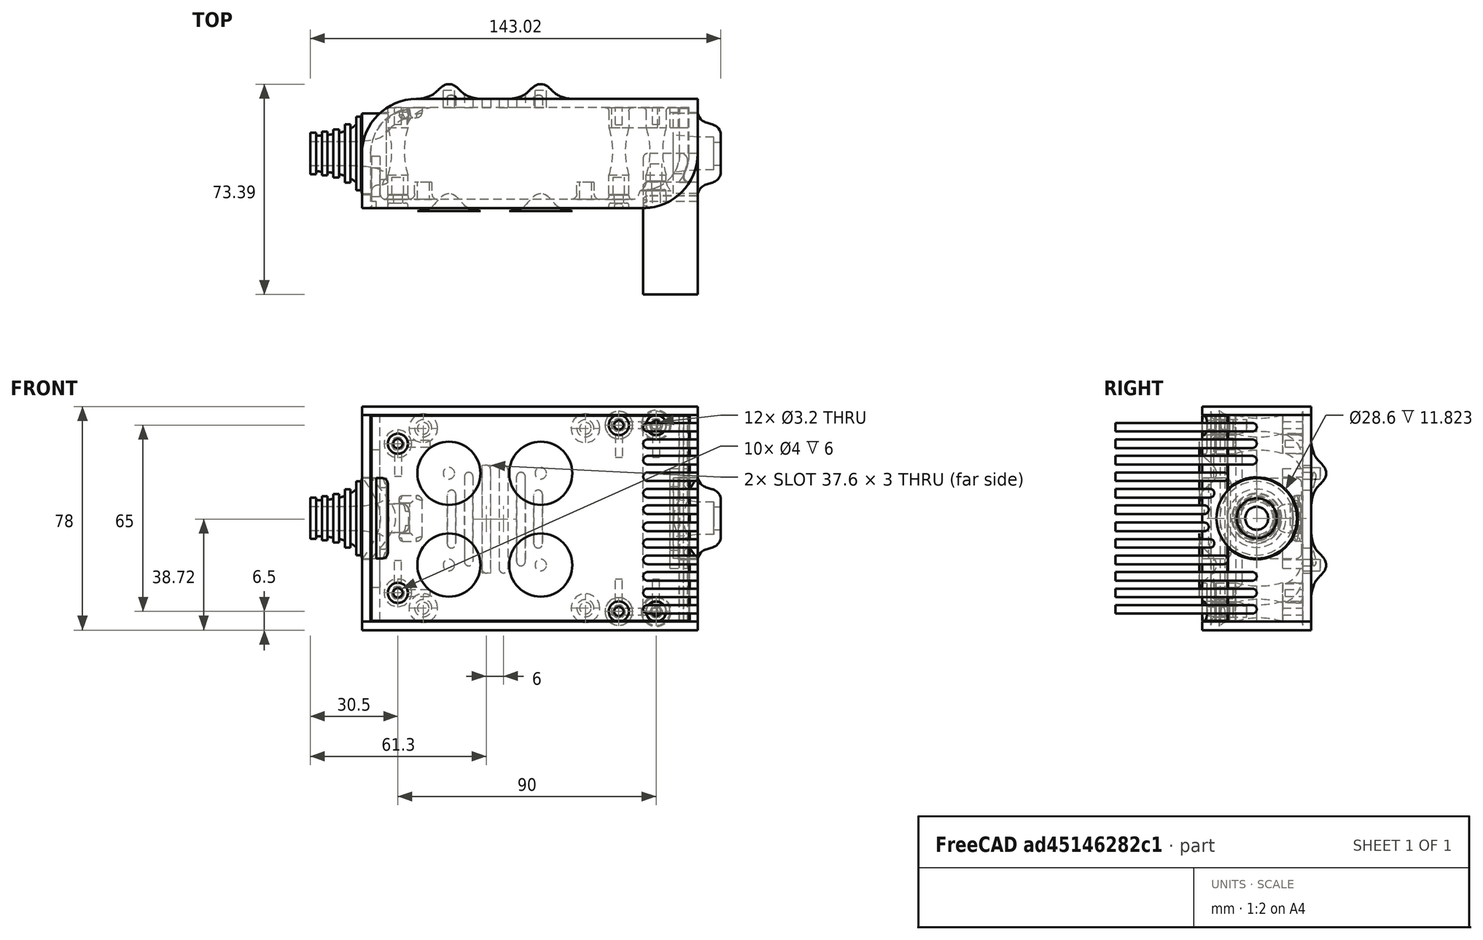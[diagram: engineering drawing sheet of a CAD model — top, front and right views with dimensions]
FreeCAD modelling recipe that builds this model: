
FCSTD DOCUMENT  (FreeCAD 0.19R0.19.2)
Label: enclosure_116
License: All rights reserved
LicenseURL: http://en.wikipedia.org/wiki/All_rights_reserved
objects: Part::Feature×72, Part::Revolution×72, Part::MultiFuse×53, Sketcher::SketchObject×31, Part::Fillet×23, Part::Cylinder×22, Part::Extrusion×20, Part::Cut×20, Part::Box×12, App::MeasureDistance×4
note: 325 computed .brp shape members not serialized (recipe doc carries the construction recipe); baked Part::Feature solids carry a one-line shape summary decoded from their .brp

FEATURE [Sketcher::SketchObject] Sketch  label="topSketch"
  FullyConstrained = true
  sketch-geometry (13):
    g0: LineSegment StartX=117 StartY=19 StartZ=0 EndX=117 EndY=38 EndZ=0
    g1: ArcOfCircle CenterX=98 CenterY=19 CenterZ=0 NormalX=0 NormalY=0 NormalZ=1 AngleXU=0 Radius=19 StartAngle=5.7297 EndAngle=6.28319
    g2: LineSegment StartX=0 StartY=3 StartZ=0 EndX=0 EndY=19 EndZ=0
    g3: LineSegment StartX=19 StartY=38 StartZ=0 EndX=117 EndY=38 EndZ=0
    g4: ArcOfCircle CenterX=19 CenterY=19 CenterZ=0 NormalX=0 NormalY=0 NormalZ=1 AngleXU=0 Radius=19 StartAngle=1.5708 EndAngle=3.14159
    g5: ArcOfCircle CenterX=19 CenterY=19 CenterZ=0 NormalX=0 NormalY=0 NormalZ=1 AngleXU=0 Radius=16 StartAngle=1.5708 EndAngle=3.14159
    g6: ArcOfCircle CenterX=98 CenterY=19 CenterZ=0 NormalX=0 NormalY=0 NormalZ=1 AngleXU=0 Radius=16 StartAngle=5.60905 EndAngle=6.28319
    g7: LineSegment StartX=114 StartY=19 StartZ=0 EndX=114 EndY=35 EndZ=0
    g8: LineSegment StartX=110.5 StartY=9.01251 StartZ=0 EndX=114.163 EndY=9.01251 EndZ=0
    g9: LineSegment StartX=114 StartY=35 StartZ=0 EndX=19 EndY=35 EndZ=0
    g10: LineSegment StartX=0 StartY=3 StartZ=0 EndX=0 EndY=0 EndZ=0
    g11: LineSegment StartX=3 StartY=0 StartZ=0 EndX=0 EndY=0 EndZ=0
    g12: LineSegment StartX=3 StartY=19 StartZ=0 EndX=3 EndY=0 EndZ=0
  constraints (33):
    c: Vertical(g0)
    c: Distance(g0) = 19
    c: Block(g0)
    c: Coincident(g1,g0)
    c: Block(g1)
    c: Vertical(g2)
    c: Block(g2)
    c: Coincident(g3,g0)
    c: Horizontal(g3)
    c: Distance(g3) = 98
    c: Coincident(g4,g3)
    c: Coincident(g4,g2)
    c: Block(g4)
    c: Coincident(g5,g4)
    c: Coincident(g6,g1)
    c: Block(g6)
    c: Block(g5)
    c: Coincident(g7,g6)
    c: Vertical(g7)
    c: Coincident(g8,g6)
    c: Coincident(g8,g1)
    c: Coincident(g9,g7)
    c: Coincident(g9,g5)
    c: Horizontal(g9)
    c: Tangent(g9,g5)
    c: Coincident(g10,g2)
    c: Distance(g10) = 3
    c: Vertical(g10)
    c: Coincident(g11,g10)
    c: Horizontal(g11)
    c: Coincident(g12,g5)
    c: Coincident(g12,g11)
    c: Vertical(g12)
FEATURE [Sketcher::SketchObject] Sketch001  label="bottomSketch"
  FullyConstrained = true
  sketch-geometry (32):
    g0: LineSegment StartX=3.3 StartY=-6.03275e-07 StartZ=0 EndX=98 EndY=-6.03275e-07 EndZ=0
    g1: ArcOfCircle CenterX=98 CenterY=19 CenterZ=0 NormalX=0 NormalY=0 NormalZ=1 AngleXU=0 Radius=19 StartAngle=4.71239 EndAngle=5.71103
    g2: LineSegment StartX=6.3 StartY=8 StartZ=0 EndX=3.3 EndY=8 EndZ=0
    g3: LineSegment StartX=3.3 StartY=8 StartZ=0 EndX=3.3 EndY=-6.03275e-07 EndZ=0
    g4: ArcOfCircle CenterX=8.3 CenterY=5 CenterZ=0 NormalX=0 NormalY=0 NormalZ=1 AngleXU=0 Radius=2 StartAngle=3.14159 EndAngle=4.71239
    g5: LineSegment StartX=6.3 StartY=8 StartZ=0 EndX=6.3 EndY=5 EndZ=0
    g6: ArcOfCircle CenterX=98 CenterY=19 CenterZ=0 NormalX=0 NormalY=0 NormalZ=1 AngleXU=0 Radius=12.7 StartAngle=4.71239 EndAngle=6.28319
    g7: LineSegment StartX=94.7 StartY=3 StartZ=0 EndX=8.3 EndY=3 EndZ=0
    g8-g12: Circle x5 (B-spline internal-alignment scaffolding for g13; pole/knot coordinates omitted)
    g13: BSplineCurve PolesCount=5 KnotsCount=3 Degree=3 IsPeriodic=0
    g14: GeomPoint X=98 Y=6.3 Z=0
    g15: GeomPoint X=96.3938 Y=4.71946 Z=0
    g16: GeomPoint X=94.7 Y=3 Z=0
    g17-g23: Circle x7 (B-spline internal-alignment scaffolding for g24; pole/knot coordinates omitted)
    g24: BSplineCurve PolesCount=7 KnotsCount=5 Degree=3 IsPeriodic=0
    g25-g29: GeomPoint x5 (B-spline internal-alignment scaffolding for g24; pole/knot coordinates omitted)
    g30: ArcOfCircle CenterX=98 CenterY=19 CenterZ=0 NormalX=0 NormalY=0 NormalZ=1 AngleXU=0 Radius=15.7 StartAngle=5.81226 EndAngle=6.28319
    g31: LineSegment StartX=110.7 StartY=19 StartZ=0 EndX=113.7 EndY=19 EndZ=0
  constraints (41):
    c: Horizontal(g0)
    c: Coincident(g1,g0)
    c: Block(g1)
    c: Horizontal(g2)
    c: Distance(g2) = 3
    c: Coincident(g3,g2)
    c: Vertical(g3)
    c: Coincident(g3,g0)
    c: Block(g4)
    c: Block(g2)
    c: Coincident(g5,g2)
    c: Coincident(g5,g4)
    c: Vertical(g5)
    c: Coincident(g6,g1)
    c: Block(g6)
    c: Coincident(g7,g4)
    c: Horizontal(g7)
    c: Block(g0)
    c: Block(g7)
    c: Block(g3)
    c: Coincident(g13,g6)
    c: Weight(g8) = 1
    c: Equal(g8, g9-g12) x4
    c: Coincident(g13,g7)
    c: InternalAlignment(g8-g12 -> g13) x5
    c: InternalAlignment(g14,g13)
    c: InternalAlignment(g15,g13)
    c: InternalAlignment(g16,g13)
    c: Block(g13)
    c: Weight(g17) = 1
    c: Equal(g17, g18-g23) x6
    c: Coincident(g24,g1)
    c: InternalAlignment(g17-g23 -> g24) x7
    c: InternalAlignment(g25-g29 -> g24) x5
    c: Block(g24)
    c: Coincident(g30,g24)
    c: Coincident(g31,g6)
    c: Coincident(g31,g30)
    c: Horizontal(g31)
    c: Block(g31)
    c: Block(g30)
FEATURE [Part::Extrusion] Extrude  label="top"
  Base = -> Sketch
  Dir = (0,0,1)
  DirMode = 2
  FaceMakerClass = Part::FaceMakerBullseye
  LengthFwd = 72
  LengthRev = 0
  Solid = true
  Symmetric = false
FEATURE [Part::Extrusion] Extrude001  label="bottom"
  Base = -> Sketch001
  Dir = (0,0,1)
  DirMode = 2
  FaceMakerClass = Part::FaceMakerBullseye
  LengthFwd = 71.4
  LengthRev = 0
  Placement = pos=(0,0,0.3) rot=(0,0,1;0rad)
  Solid = true
  Symmetric = false
FEATURE [Sketcher::SketchObject] Sketch002  label="topSketch001"
  FullyConstrained = true
  sketch-geometry (6):
    g0: LineSegment StartX=19 StartY=38 StartZ=0 EndX=117 EndY=38 EndZ=0
    g1: ArcOfCircle CenterX=19 CenterY=19 CenterZ=0 NormalX=0 NormalY=0 NormalZ=1 AngleXU=0 Radius=19 StartAngle=1.5708 EndAngle=3.14159
    g2: LineSegment StartX=117 StartY=38 StartZ=0 EndX=117 EndY=19 EndZ=0
    g3: LineSegment StartX=98 StartY=1.0161e-12 StartZ=0 EndX=5.22862e-06 EndY=1.0161e-12 EndZ=0
    g4: LineSegment StartX=5.22862e-06 StartY=19 StartZ=0 EndX=5.22862e-06 EndY=1.0161e-12 EndZ=0
    g5: ArcOfCircle CenterX=98 CenterY=19 CenterZ=0 NormalX=0 NormalY=0 NormalZ=1 AngleXU=0 Radius=19 StartAngle=4.71239 EndAngle=6.28319
  constraints (16):
    c: Horizontal(g0)
    c: Distance(g0) = 98
    c: Coincident(g1,g0)
    c: Block(g1)
    c: Coincident(g2,g0)
    c: Vertical(g2)
    c: Distance(g2) = 19
    c: Horizontal(g3)
    c: Coincident(g4,g1)
    c: Vertical(g4)
    c: Coincident(g3,g4)
    c: Block(g3)
    c: Coincident(g5,g2)
    c: Coincident(g5,g3)
    c: Block(g0)
    c: Block(g5)
FEATURE [Part::Extrusion] Extrude002  label="sideA"
  Base = -> Sketch002
  Dir = (0,0,1)
  DirMode = 2
  FaceMakerClass = Part::FaceMakerBullseye
  LengthFwd = 3
  LengthRev = 0
  Placement = pos=(0,0,-3) rot=(0,0,1;0rad)
  Solid = true
  Symmetric = false
FEATURE [Sketcher::SketchObject] Sketch003  label="topSketch002"
  FullyConstrained = true
  sketch-geometry (6):
    g0: LineSegment StartX=19 StartY=38 StartZ=0 EndX=117 EndY=38 EndZ=0
    g1: ArcOfCircle CenterX=19 CenterY=19 CenterZ=0 NormalX=0 NormalY=0 NormalZ=1 AngleXU=0 Radius=19 StartAngle=1.5708 EndAngle=3.14159
    g2: LineSegment StartX=117 StartY=38 StartZ=0 EndX=117 EndY=19 EndZ=0
    g3: LineSegment StartX=98 StartY=1.0161e-12 StartZ=0 EndX=5.22862e-06 EndY=1.0161e-12 EndZ=0
    g4: LineSegment StartX=5.22862e-06 StartY=19 StartZ=0 EndX=5.22862e-06 EndY=1.0161e-12 EndZ=0
    g5: ArcOfCircle CenterX=98 CenterY=19 CenterZ=0 NormalX=0 NormalY=0 NormalZ=1 AngleXU=0 Radius=19 StartAngle=4.71239 EndAngle=6.28319
  constraints (16):
    c: Horizontal(g0)
    c: Distance(g0) = 98
    c: Coincident(g1,g0)
    c: Block(g1)
    c: Coincident(g2,g0)
    c: Vertical(g2)
    c: Distance(g2) = 19
    c: Horizontal(g3)
    c: Coincident(g4,g1)
    c: Vertical(g4)
    c: Coincident(g3,g4)
    c: Block(g3)
    c: Coincident(g5,g2)
    c: Coincident(g5,g3)
    c: Block(g0)
    c: Block(g5)
FEATURE [Part::Extrusion] Extrude003  label="sideB"
  Base = -> Sketch003
  Dir = (0,0,1)
  DirMode = 2
  FaceMakerClass = Part::FaceMakerBullseye
  LengthFwd = 3
  LengthRev = 0
  Placement = pos=(0,0,72) rot=(0,0,1;0rad)
  Solid = true
  Symmetric = false
FEATURE [Sketcher::SketchObject] Sketch004
  FullyConstrained = true
  MapMode = 3
  Placement = pos=(0,0,0) rot=(1,0,0;1.5708rad)
  Support = -> [Extrude]
  sketch-geometry (8):
    g0: Circle CenterX=80.351 CenterY=-67.6202 CenterZ=0 NormalX=0 NormalY=0 NormalZ=1 AngleXU=0 Radius=2
    g1: Circle CenterX=80.351 CenterY=-67.6202 CenterZ=0 NormalX=0 NormalY=0 NormalZ=1 AngleXU=0 Radius=3
    g2: Circle CenterX=80.351 CenterY=-4.92017 CenterZ=0 NormalX=0 NormalY=0 NormalZ=1 AngleXU=0 Radius=2
    g3: Circle CenterX=80.351 CenterY=-4.92017 CenterZ=0 NormalX=0 NormalY=0 NormalZ=1 AngleXU=0 Radius=3
    g4: Circle CenterX=23.851 CenterY=-4.92017 CenterZ=0 NormalX=0 NormalY=0 NormalZ=1 AngleXU=0 Radius=2
    g5: Circle CenterX=23.851 CenterY=-4.92017 CenterZ=0 NormalX=0 NormalY=0 NormalZ=1 AngleXU=0 Radius=3
    g6: Circle CenterX=23.851 CenterY=-67.6202 CenterZ=0 NormalX=0 NormalY=0 NormalZ=1 AngleXU=0 Radius=2
    g7: Circle CenterX=23.851 CenterY=-67.6202 CenterZ=0 NormalX=0 NormalY=0 NormalZ=1 AngleXU=0 Radius=3
  constraints (8):
    c: Block(g3)
    c: Block(g2)
    c: Block(g1)
    c: Block(g0)
    c: Block(g6)
    c: Block(g7)
    c: Block(g4)
    c: Block(g5)
FEATURE [Part::Extrusion] Extrude004
  Base = -> Sketch004
  Dir = (0,-1,2e-16)
  DirMode = 2
  FaceMakerClass = Part::FaceMakerBullseye
  LengthFwd = 6
  LengthRev = 0
  Placement = pos=(0,9,0) rot=(0,0,1;0rad)
  Solid = true
  Symmetric = false
FEATURE [Sketcher::SketchObject] Sketch005
  FullyConstrained = true
  MapMode = 3
  Placement = pos=(0,0,0) rot=(1,0,0;1.5708rad)
  Support = -> [Extrude]
  sketch-geometry (8):
    g0: Circle CenterX=80.351 CenterY=-67.6202 CenterZ=0 NormalX=0 NormalY=0 NormalZ=1 AngleXU=0 Radius=3
    g1: Circle CenterX=80.351 CenterY=-4.92017 CenterZ=0 NormalX=0 NormalY=0 NormalZ=1 AngleXU=0 Radius=3
    g2: Circle CenterX=23.851 CenterY=-4.92017 CenterZ=0 NormalX=0 NormalY=0 NormalZ=1 AngleXU=0 Radius=3
    g3: Circle CenterX=23.851 CenterY=-67.6202 CenterZ=0 NormalX=0 NormalY=0 NormalZ=1 AngleXU=0 Radius=3
    g4: Circle CenterX=23.851 CenterY=-67.6202 CenterZ=0 NormalX=0 NormalY=0 NormalZ=1 AngleXU=0 Radius=5
    g5: Circle CenterX=80.351 CenterY=-67.6202 CenterZ=0 NormalX=0 NormalY=0 NormalZ=1 AngleXU=0 Radius=5
    g6: Circle CenterX=23.851 CenterY=-4.92017 CenterZ=0 NormalX=0 NormalY=0 NormalZ=1 AngleXU=0 Radius=5
    g7: Circle CenterX=80.351 CenterY=-4.92017 CenterZ=0 NormalX=0 NormalY=0 NormalZ=1 AngleXU=0 Radius=5
  constraints (8):
    c: Block(g1)
    c: Block(g0)
    c: Block(g3)
    c: Block(g2)
    c: Block(g5)
    c: Block(g4)
    c: Block(g6)
    c: Block(g7)
FEATURE [Part::Extrusion] Extrude005
  Base = -> Sketch005
  Dir = (0,-1,2e-16)
  DirMode = 2
  FaceMakerClass = Part::FaceMakerBullseye
  LengthFwd = 2
  LengthRev = 0
  Solid = true
  Symmetric = false
FEATURE [Sketcher::SketchObject] Sketch006
  FullyConstrained = true
  MapMode = 3
  Placement = pos=(0,0,0) rot=(1,0,0;1.5708rad)
  sketch-geometry (8):
    g0: Circle CenterX=80.351 CenterY=-67.6202 CenterZ=0 NormalX=0 NormalY=0 NormalZ=1 AngleXU=0 Radius=3
    g1: Circle CenterX=80.351 CenterY=-4.92017 CenterZ=0 NormalX=0 NormalY=0 NormalZ=1 AngleXU=0 Radius=3
    g2: Circle CenterX=23.851 CenterY=-4.92017 CenterZ=0 NormalX=0 NormalY=0 NormalZ=1 AngleXU=0 Radius=3
    g3: Circle CenterX=23.851 CenterY=-67.6202 CenterZ=0 NormalX=0 NormalY=0 NormalZ=1 AngleXU=0 Radius=3
    g4: Circle CenterX=23.851 CenterY=-67.6202 CenterZ=0 NormalX=0 NormalY=0 NormalZ=1 AngleXU=0 Radius=5
    g5: Circle CenterX=80.351 CenterY=-67.6202 CenterZ=0 NormalX=0 NormalY=0 NormalZ=1 AngleXU=0 Radius=5
    g6: Circle CenterX=23.851 CenterY=-4.92017 CenterZ=0 NormalX=0 NormalY=0 NormalZ=1 AngleXU=0 Radius=5
    g7: Circle CenterX=80.351 CenterY=-4.92017 CenterZ=0 NormalX=0 NormalY=0 NormalZ=1 AngleXU=0 Radius=5
  constraints (8):
    c: Block(g1)
    c: Block(g0)
    c: Block(g3)
    c: Block(g2)
    c: Block(g5)
    c: Block(g4)
    c: Block(g6)
    c: Block(g7)
FEATURE [Part::Extrusion] Extrude007
  Base = -> Sketch006
  Dir = (0,-1,2e-16)
  DirMode = 2
  FaceMakerClass = Part::FaceMakerBullseye
  LengthFwd = 2
  LengthRev = 0
  Solid = true
  Symmetric = false
FEATURE [Part::Fillet] Fillet
  Base = -> Extrude007
  Edges = 4 edges r=1.99: [Edge6,Edge12,Edge18,Edge24]
FEATURE [Part::Cut] Cut
  Base = -> Extrude005
  Placement = pos=(0,5,0) rot=(0,0,1;0rad)
  Tool = -> Fillet
FEATURE [Part::MultiFuse] Fusion  label="pCBScrews"
  Placement = pos=(-2.5,0,72.3) rot=(0,0,1;0rad)
  Shapes = -> [Extrude004,Cut]
FEATURE [App::MeasureDistance] Distance  label="Distance: 0.69 mm"
  Distance = 0.685967
  P1 = (24.0138,2.9647,0.3)
  P2 = (23.8901,3,-0.373787)
FEATURE [App::MeasureDistance] Distance001  label="Distance: 0.53 mm"
  Distance = 0.533607
  P1 = (80.2939,3,72.2334)
  P2 = (80.281,2.99661,71.7)
FEATURE [Part::Fillet] Fillet001
  Base = -> Extrude001
  Edges = 1 edges r=2.4: [Edge17]
FEATURE [Part::Fillet] Fillet002  label="bottom001"
  Base = -> Fillet001
  Edges = 1 edges r=2.4: [Edge36]
FEATURE [Part::Fillet] Fillet003  label="top001"
  Base = -> Extrude
  Edges = 1 edges r=2: [Edge1]
FEATURE [Sketcher::SketchObject] Sketch007
  FullyConstrained = true
  sketch-geometry (16):
    g0: LineSegment StartX=4 StartY=0 StartZ=0 EndX=4 EndY=2.4 EndZ=0
    g1: LineSegment StartX=4 StartY=2.4 StartZ=0 EndX=7 EndY=2.4 EndZ=0
    g2: LineSegment StartX=4 StartY=0 StartZ=0 EndX=5.7 EndY=0 EndZ=0
    g3: LineSegment StartX=5.7 StartY=0 StartZ=0 EndX=5.7 EndY=-5.6 EndZ=0
    g4-g8: Circle x5 (B-spline internal-alignment scaffolding for g9; pole/knot coordinates omitted)
    g9: BSplineCurve PolesCount=5 KnotsCount=3 Degree=3 IsPeriodic=0
    g10: GeomPoint X=7 Y=2.4 Z=0
    g11: GeomPoint X=10.4582 Y=-1.55472 Z=0
    g12: GeomPoint X=14 Y=-5.6 Z=0
    g13: LineSegment StartX=14 StartY=-5.6 StartZ=0 EndX=14 EndY=-14.1 EndZ=0
    g14: LineSegment StartX=14 StartY=-14.1 StartZ=0 EndX=6.5 EndY=-14.1 EndZ=0
    g15: LineSegment StartX=5.7 StartY=-5.6 StartZ=0 EndX=6.5 EndY=-14.1 EndZ=0
  constraints (28):
    c: Distance(g0) = 2.4
    c: Vertical(g0)
    c: Block(g0)
    c: Coincident(g1,g0)
    c: Horizontal(g1)
    c: Distance(g1) = 3
    c: Coincident(g2,g0)
    c: Horizontal(g2)
    c: Distance(g2) = 1.7
    c: Coincident(g3,g2)
    c: Vertical(g3)
    c: Distance(g3) = 5.6
    c: Coincident(g9,g1)
    c: Weight(g4) = 1
    c: Equal(g4, g5-g8) x4
    c: InternalAlignment(g4-g8 -> g9) x5
    c: InternalAlignment(g10,g9)
    c: InternalAlignment(g11,g9)
    c: InternalAlignment(g12,g9)
    c: Block(g9)
    c: Coincident(g13,g9)
    c: Vertical(g13)
    c: Distance(g13) = 8.5
    c: Coincident(g14,g13)
    c: Horizontal(g14)
    c: Distance(g14) = 7.5
    c: Coincident(g15,g3)
    c: Coincident(g15,g14)
FEATURE [Part::Feature] Face
  shape: bbox 10 x 16.5 x 2e-07 mm, 1 faces, 0 solids (baked)
FEATURE [Part::Revolution] Revolve  label="plugHousing"
  Angle = 360
  Axis = (0,1,0)
  Base = (0,0,0)
  FaceMakerClass = Part::FaceMakerBullseye
  Placement = pos=(0,0,36.15) rot=(0,0,1;0rad)
  Solid = false
  Source = -> Face
  Symmetric = false
FEATURE [Part::Feature] Face001
  shape: bbox 10 x 16.5 x 2e-07 mm, 1 faces, 0 solids (baked)
FEATURE [Part::Revolution] Revolve001  label="plugHousing001"
  Angle = 360
  Axis = (0,1,0)
  Base = (0,0,0)
  FaceMakerClass = Part::FaceMakerBullseye
  Placement = pos=(0,0,36.15) rot=(0,0,1;0rad)
  Solid = false
  Source = -> Face001
  Symmetric = false
FEATURE [Part::MultiFuse] Fusion001  label="plugHousing002"
  Placement = pos=(0,0,0) rot=(0,0,1;1.5708rad)
  Shapes = -> [Revolve001,Revolve]
FEATURE [Part::Feature] Face002
  shape: bbox 10 x 16.5 x 2e-07 mm, 1 faces, 0 solids (baked)
FEATURE [Part::Revolution] Revolve003  label="plugHousing005"
  Angle = 360
  Axis = (0,1,0)
  Base = (0,0,0)
  FaceMakerClass = Part::FaceMakerBullseye
  Placement = pos=(0,0,36.15) rot=(0,0,1;0rad)
  Solid = false
  Source = -> Face002
  Symmetric = false
FEATURE [Part::Feature] Face003
  shape: bbox 10 x 16.5 x 2e-07 mm, 1 faces, 0 solids (baked)
FEATURE [Part::Revolution] Revolve002  label="plugHousing003"
  Angle = 360
  Axis = (0,1,0)
  Base = (0,0,0)
  FaceMakerClass = Part::FaceMakerBullseye
  Placement = pos=(0,0,36.15) rot=(0,0,1;0rad)
  Solid = false
  Source = -> Face003
  Symmetric = false
FEATURE [Part::MultiFuse] Fusion002  label="plugHousing004"
  Placement = pos=(0,0,0) rot=(0,0,1;1.5708rad)
  Shapes = -> [Revolve002,Revolve003]
FEATURE [Part::MultiFuse] Fusion003  label="plugHousing006"
  Placement = pos=(0,19,0) rot=(0,0,1;3.14159rad)
  Shapes = -> [Fusion002,Fusion001]
FEATURE [Part::Feature] Face004
  shape: bbox 10 x 16.5 x 2e-07 mm, 1 faces, 0 solids (baked)
FEATURE [Part::Revolution] Revolve006  label="plugHousing010"
  Angle = 360
  Axis = (0,1,0)
  Base = (0,0,0)
  FaceMakerClass = Part::FaceMakerBullseye
  Placement = pos=(0,0,36.15) rot=(0,0,1;0rad)
  Solid = false
  Source = -> Face004
  Symmetric = false
FEATURE [Part::Feature] Face005
  shape: bbox 10 x 16.5 x 2e-07 mm, 1 faces, 0 solids (baked)
FEATURE [Part::Revolution] Revolve007  label="plugHousing011"
  Angle = 360
  Axis = (0,1,0)
  Base = (0,0,0)
  FaceMakerClass = Part::FaceMakerBullseye
  Placement = pos=(0,0,36.15) rot=(0,0,1;0rad)
  Solid = false
  Source = -> Face005
  Symmetric = false
FEATURE [Part::Feature] Face006
  shape: bbox 10 x 16.5 x 2e-07 mm, 1 faces, 0 solids (baked)
FEATURE [Part::Revolution] Revolve004  label="plugHousing007"
  Angle = 360
  Axis = (0,1,0)
  Base = (0,0,0)
  FaceMakerClass = Part::FaceMakerBullseye
  Placement = pos=(0,0,36.15) rot=(0,0,1;0rad)
  Solid = false
  Source = -> Face006
  Symmetric = false
FEATURE [Part::MultiFuse] Fusion004  label="plugHousing009"
  Placement = pos=(0,0,0) rot=(0,0,1;1.5708rad)
  Shapes = -> [Revolve004,Revolve007]
FEATURE [Part::Feature] Face007
  shape: bbox 10 x 16.5 x 2e-07 mm, 1 faces, 0 solids (baked)
FEATURE [Part::Revolution] Revolve005  label="plugHousing008"
  Angle = 360
  Axis = (0,1,0)
  Base = (0,0,0)
  FaceMakerClass = Part::FaceMakerBullseye
  Placement = pos=(0,0,36.15) rot=(0,0,1;0rad)
  Solid = false
  Source = -> Face007
  Symmetric = false
FEATURE [Part::MultiFuse] Fusion005  label="plugHousing012"
  Placement = pos=(0,0,0) rot=(0,0,1;1.5708rad)
  Shapes = -> [Revolve006,Revolve005]
FEATURE [Part::MultiFuse] Fusion006  label="plugHousing013"
  Placement = pos=(0,19,0) rot=(0,0,1;3.14159rad)
  Shapes = -> [Fusion005,Fusion004]
FEATURE [Part::MultiFuse] Fusion007  label="plugHousing014"
  Placement = pos=(122.621,0,-0.15) rot=(0,0,1;0rad)
  Shapes = -> [Fusion003,Fusion006]
FEATURE [Part::Cylinder] Cylinder002
  Angle = 360
  AttacherType = Attacher::AttachEngine3D
  Height = 20
  Placement = pos=(0,0,36.15) rot=(0,0,1;0rad)
  Radius = 4
FEATURE [Part::Cylinder] Cylinder003
  Angle = 360
  AttacherType = Attacher::AttachEngine3D
  Height = 10
  Placement = pos=(0,0,36.15) rot=(0,0,1;0rad)
  Radius = 4
FEATURE [Part::MultiFuse] Fusion009  label="removeToCreateHoleForPlugHousing"
  Placement = pos=(70,19,36.15) rot=(0,1,0;1.5708rad)
  Shapes = -> [Cylinder002,Cylinder003]
FEATURE [Part::Cylinder] Cylinder004
  Angle = 360
  AttacherType = Attacher::AttachEngine3D
  Height = 20
  Placement = pos=(0,0,36.15) rot=(0,0,1;0rad)
  Radius = 4
FEATURE [Part::Cylinder] Cylinder005
  Angle = 360
  AttacherType = Attacher::AttachEngine3D
  Height = 10
  Placement = pos=(0,0,36.15) rot=(0,0,1;0rad)
  Radius = 4
FEATURE [Part::MultiFuse] Fusion010  label="removeToCreateHoleForPlugHousing001"
  Placement = pos=(70,19,36.15) rot=(0,1,0;1.5708rad)
  Shapes = -> [Cylinder004,Cylinder005]
FEATURE [Part::Cut] Cut001
  Base = -> Fillet003
  Tool = -> Fusion010
FEATURE [Part::Cut] Cut002  label="Bottom"
  Base = -> Fillet002
  Tool = -> Fusion009
FEATURE [Part::Feature] Face008
  shape: bbox 10 x 16.5 x 2e-07 mm, 1 faces, 0 solids (baked)
FEATURE [Part::Revolution] Revolve011  label="plugHousing021"
  Angle = 360
  Axis = (0,1,0)
  Base = (0,0,0)
  FaceMakerClass = Part::FaceMakerBullseye
  Placement = pos=(0,0,36.15) rot=(0,0,1;0rad)
  Solid = false
  Source = -> Face008
  Symmetric = false
FEATURE [Part::Feature] Face009
  shape: bbox 10 x 16.5 x 2e-07 mm, 1 faces, 0 solids (baked)
FEATURE [Part::Revolution] Revolve012  label="plugHousing022"
  Angle = 360
  Axis = (0,1,0)
  Base = (0,0,0)
  FaceMakerClass = Part::FaceMakerBullseye
  Placement = pos=(0,0,36.15) rot=(0,0,1;0rad)
  Solid = false
  Source = -> Face009
  Symmetric = false
FEATURE [Part::Feature] Face010 .. Face013  x4 (patterned run collapsed; names and placements below)
  shape: bbox 10 x 16.5 x 2e-07 mm, 1 faces, 0 solids (baked)
FEATURE [Part::Revolution] Revolve015  label="plugHousing027"
  Angle = 360
  Axis = (0,1,0)
  Base = (0,0,0)
  FaceMakerClass = Part::FaceMakerBullseye
  Placement = pos=(0,0,36.15) rot=(0,0,1;0rad)
  Solid = false
  Source = -> Face013
  Symmetric = false
FEATURE [Part::Feature] Face014
  shape: bbox 10 x 16.5 x 2e-07 mm, 1 faces, 0 solids (baked)
FEATURE [Part::Feature] Face015
  shape: bbox 10 x 16.5 x 2e-07 mm, 1 faces, 0 solids (baked)
FEATURE [Part::Feature] Face016
  shape: bbox 10 x 16.5 x 2e-07 mm, 1 faces, 0 solids (baked)
FEATURE [Part::Revolution] Revolve019  label="plugHousing033"
  Angle = 360
  Axis = (0,1,0)
  Base = (0,0,0)
  FaceMakerClass = Part::FaceMakerBullseye
  Placement = pos=(0,0,36.15) rot=(0,0,1;0rad)
  Solid = false
  Source = -> Face016
  Symmetric = false
FEATURE [Part::Feature] Face017
  shape: bbox 10 x 16.5 x 2e-07 mm, 1 faces, 0 solids (baked)
FEATURE [Part::Revolution] Revolve020  label="plugHousing034"
  Angle = 360
  Axis = (0,1,0)
  Base = (0,0,0)
  FaceMakerClass = Part::FaceMakerBullseye
  Placement = pos=(0,0,36.15) rot=(0,0,1;0rad)
  Solid = false
  Source = -> Face017
  Symmetric = false
FEATURE [Part::Feature] Face018
  shape: bbox 10 x 16.5 x 2e-07 mm, 1 faces, 0 solids (baked)
FEATURE [Part::Revolution] Revolve016  label="plugHousing030"
  Angle = 360
  Axis = (0,1,0)
  Base = (0,0,0)
  FaceMakerClass = Part::FaceMakerBullseye
  Placement = pos=(0,0,36.15) rot=(0,0,1;0rad)
  Solid = false
  Source = -> Face018
  Symmetric = false
FEATURE [Part::MultiFuse] Fusion020  label="plugHousing038"
  Placement = pos=(0,0,0) rot=(0,0,1;1.5708rad)
  Shapes = -> [Revolve016,Revolve020]
FEATURE [Part::Feature] Face019
  shape: bbox 10 x 16.5 x 2e-07 mm, 1 faces, 0 solids (baked)
FEATURE [Part::Feature] Face020
  shape: bbox 10 x 16.5 x 2e-07 mm, 1 faces, 0 solids (baked)
FEATURE [Part::Revolution] Revolve017  label="plugHousing031"
  Angle = 360
  Axis = (0,1,0)
  Base = (0,0,0)
  FaceMakerClass = Part::FaceMakerBullseye
  Placement = pos=(0,0,36.15) rot=(0,0,1;0rad)
  Solid = false
  Source = -> Face020
  Symmetric = false
FEATURE [Part::MultiFuse] Fusion021  label="plugHousing039"
  Placement = pos=(0,0,0) rot=(0,0,1;1.5708rad)
  Shapes = -> [Revolve019,Revolve017]
FEATURE [Part::MultiFuse] Fusion023  label="plugHousing041"
  Placement = pos=(0,19,0) rot=(0,0,1;3.14159rad)
  Shapes = -> [Fusion021,Fusion020]
FEATURE [Part::Revolution] Revolve022  label="plugHousing043"
  Angle = 360
  Axis = (0,1,0)
  Base = (0,0,0)
  FaceMakerClass = Part::FaceMakerBullseye
  Placement = pos=(0,0,36.15) rot=(0,0,1;0rad)
  Solid = false
  Source = -> Face019
  Symmetric = false
FEATURE [Part::Feature] Face021
  shape: bbox 10 x 16.5 x 2e-07 mm, 1 faces, 0 solids (baked)
FEATURE [Part::Revolution] Revolve023  label="plugHousing044"
  Angle = 360
  Axis = (0,1,0)
  Base = (0,0,0)
  FaceMakerClass = Part::FaceMakerBullseye
  Placement = pos=(0,0,36.15) rot=(0,0,1;0rad)
  Solid = false
  Source = -> Face021
  Symmetric = false
FEATURE [Part::Feature] Face022
  shape: bbox 10 x 16.5 x 2e-07 mm, 1 faces, 0 solids (baked)
FEATURE [Part::Revolution] Revolve018  label="plugHousing032"
  Angle = 360
  Axis = (0,1,0)
  Base = (0,0,0)
  FaceMakerClass = Part::FaceMakerBullseye
  Placement = pos=(0,0,36.15) rot=(0,0,1;0rad)
  Solid = false
  Source = -> Face022
  Symmetric = false
FEATURE [Part::MultiFuse] Fusion022  label="plugHousing040"
  Placement = pos=(0,0,0) rot=(0,0,1;1.5708rad)
  Shapes = -> [Revolve018,Revolve023]
FEATURE [Part::Feature] Face023
  shape: bbox 10 x 16.5 x 2e-07 mm, 1 faces, 0 solids (baked)
FEATURE [Part::Revolution] Revolve021  label="plugHousing035"
  Angle = 360
  Axis = (0,1,0)
  Base = (0,0,0)
  FaceMakerClass = Part::FaceMakerBullseye
  Placement = pos=(0,0,36.15) rot=(0,0,1;0rad)
  Solid = false
  Source = -> Face023
  Symmetric = false
FEATURE [Part::MultiFuse] Fusion018  label="plugHousing036"
  Placement = pos=(0,0,0) rot=(0,0,1;1.5708rad)
  Shapes = -> [Revolve022,Revolve021]
FEATURE [Part::MultiFuse] Fusion019  label="plugHousing037"
  Placement = pos=(0,19,0) rot=(0,0,1;3.14159rad)
  Shapes = -> [Fusion018,Fusion022]
FEATURE [Part::MultiFuse] Fusion024  label="plugHousing042"
  Placement = pos=(122.621,0,-0.15) rot=(0,0,1;0rad)
  Shapes = -> [Fusion023,Fusion019]
FEATURE [Part::Cylinder] Cylinder006
  Angle = 360
  AttacherType = Attacher::AttachEngine3D
  Height = 20
  Placement = pos=(0,0,36.15) rot=(0,0,1;0rad)
  Radius = 14.3
FEATURE [Part::Cylinder] Cylinder007
  Angle = 360
  AttacherType = Attacher::AttachEngine3D
  Height = 10
  Placement = pos=(0,0,36.15) rot=(0,0,1;0rad)
  Radius = 4
FEATURE [Part::MultiFuse] Fusion026  label="removeToCreteHoleForPlugHousing"
  Placement = pos=(70,19,36) rot=(0,1,0;1.5708rad)
  Shapes = -> [Cylinder006,Cylinder007]
FEATURE [Part::Box] Box001  label="Cube001"
  AttacherType = Attacher::AttachEngine3D
  Height = 28
  Length = 3
  Placement = pos=(110.7,19,22) rot=(0,0,1;0rad)
  Width = 15.7
FEATURE [Part::Cut] Cut003  label="top002"
  Base = -> Cut001
  Tool = -> Fusion007
FEATURE [Part::Revolution] Revolve008  label="plugHousing015"
  Angle = 360
  Axis = (0,1,0)
  Base = (0,0,0)
  FaceMakerClass = Part::FaceMakerBullseye
  Placement = pos=(0,0,36.15) rot=(0,0,1;0rad)
  Solid = false
  Source = -> Face010
  Symmetric = false
FEATURE [Part::MultiFuse] Fusion013  label="plugHousing020"
  Placement = pos=(0,0,0) rot=(0,0,1;1.5708rad)
  Shapes = -> [Revolve008,Revolve012]
FEATURE [Part::Cut] Cut004  label="top003"
  Base = -> Cut003
  Placement = pos=(1,0,0) rot=(0,0,1;0rad)
  Tool = -> Fusion026
FEATURE [Part::Cylinder] Cylinder008
  Angle = 360
  AttacherType = Attacher::AttachEngine3D
  Height = 20
  Placement = pos=(0,0,36.15) rot=(0,0,1;0rad)
  Radius = 10.3
FEATURE [Part::Cylinder] Cylinder009
  Angle = 360
  AttacherType = Attacher::AttachEngine3D
  Height = 10
  Placement = pos=(0,0,36.15) rot=(0,0,1;0rad)
  Radius = 4
FEATURE [Part::MultiFuse] Fusion027  label="removeToCreteHoleForPlugHousing001"
  Placement = pos=(70,19,36) rot=(0,1,0;1.5708rad)
  Shapes = -> [Cylinder008,Cylinder009]
FEATURE [Part::Cut] Cut005  label="plugHousingTab"
  Base = -> Box001
  Tool = -> Fusion027
FEATURE [Part::MultiFuse] Fusion028  label="plugHousing045"
  Shapes = -> [Fusion024,Cut005]
FEATURE [Part::Box] Box002  label="Cube002"
  AttacherType = Attacher::AttachEngine3D
  Height = 28.8
  Length = 3
  Placement = pos=(107.3,28,21.6) rot=(0,0,1;0rad)
  Width = 7
FEATURE [Part::Box] Box003  label="Cube003"
  AttacherType = Attacher::AttachEngine3D
  Height = 3
  Length = 6.4
  Placement = pos=(107.3,28,18.6) rot=(0,0,1;0rad)
  Width = 7
FEATURE [Part::Box] Box004  label="Cube004"
  AttacherType = Attacher::AttachEngine3D
  Height = 3
  Length = 6.4
  Placement = pos=(107.3,28,50.4) rot=(0,0,1;0rad)
  Width = 7
FEATURE [Part::MultiFuse] Fusion029  label="plugHousingBracketHolder"
  Shapes = -> [Box004,Box002,Box003]
FEATURE [Part::Cylinder] Cylinder010
  Angle = 360
  AttacherType = Attacher::AttachEngine3D
  Height = 20
  Placement = pos=(0,0,36.15) rot=(0,0,1;0rad)
  Radius = 14.3
FEATURE [Part::Cylinder] Cylinder011
  Angle = 360
  AttacherType = Attacher::AttachEngine3D
  Height = 10
  Placement = pos=(0,0,36.15) rot=(0,0,1;0rad)
  Radius = 4
FEATURE [Part::MultiFuse] Fusion030  label="removeToCreteHoleForPlugHousing002"
  Placement = pos=(70,19,36) rot=(0,1,0;1.5708rad)
  Shapes = -> [Cylinder010,Cylinder011]
FEATURE [Part::Cut] Cut006  label="plugHousingBracketHolder001"
  Base = -> Fusion029
  Tool = -> Fusion030
FEATURE [Part::Cylinder] Cylinder012
  Angle = 360
  AttacherType = Attacher::AttachEngine3D
  Height = 20
  Placement = pos=(0,0,36.15) rot=(0,0,1;0rad)
  Radius = 7
FEATURE [Part::Cylinder] Cylinder013
  Angle = 360
  AttacherType = Attacher::AttachEngine3D
  Height = 10
  Placement = pos=(0,0,36.15) rot=(0,0,1;0rad)
  Radius = 4
FEATURE [Part::MultiFuse] Fusion032  label="removeToCreteHoleForPlugHousing003"
  Placement = pos=(70,19,36) rot=(0,1,0;1.5708rad)
  Shapes = -> [Cylinder012,Cylinder013]
FEATURE [Part::Cut] Cut007  label="bottom002"
  Base = -> Cut002
  Tool = -> Fusion032
FEATURE [Sketcher::SketchObject] Sketch008
  FullyConstrained = true
  sketch-geometry (54):
    g0: LineSegment StartX=-4.2 StartY=0 StartZ=0 EndX=-6.2 EndY=0 EndZ=0
    g1: LineSegment StartX=-14 StartY=-18 StartZ=0 EndX=-14 EndY=-26.5 EndZ=0
    g2: LineSegment StartX=-4.2 StartY=0 StartZ=0 EndX=-4.2 EndY=-13.4877 EndZ=0
    g3: Circle CenterX=-4.2 CenterY=-13.4877 CenterZ=0 NormalX=0 NormalY=0 NormalZ=1 AngleXU=0 Radius=1
    g4: Circle CenterX=-4.2 CenterY=-26.5 CenterZ=0 NormalX=0 NormalY=0 NormalZ=1 AngleXU=0 Radius=1
    g5: Circle CenterX=-8.2 CenterY=-26.5 CenterZ=0 NormalX=0 NormalY=0 NormalZ=1 AngleXU=0 Radius=1
    g6: BSplineCurve PolesCount=3 KnotsCount=2 Degree=2 IsPeriodic=0
    g7: GeomPoint X=-4.2 Y=-13.4877 Z=0
    g8: GeomPoint X=-8.2 Y=-26.5 Z=0
    g9: LineSegment StartX=-14 StartY=-26.5 StartZ=0 EndX=-8.2 EndY=-26.5 EndZ=0
    g10: LineSegment StartX=-10.15 StartY=-12 StartZ=0 EndX=-10.15 EndY=-14 EndZ=0
    g11: LineSegment StartX=-12.8401 StartY=-16 StartZ=0 EndX=-10.1571 EndY=-16 EndZ=0
    g12: LineSegment StartX=-10.15 StartY=-14 StartZ=0 EndX=-8.70761 EndY=-14 EndZ=0
    g13: LineSegment StartX=-12.8401 StartY=-16 StartZ=0 EndX=-12.8401 EndY=-17.6958 EndZ=0
    g14: LineSegment StartX=-10.15 StartY=-12 StartZ=0 EndX=-7.79258 EndY=-12 EndZ=0
    g15: Circle CenterX=-6.2215 CenterY=-2 CenterZ=0 NormalX=0 NormalY=0 NormalZ=1 AngleXU=0 Radius=1
    g16: Circle CenterX=-6.22762 CenterY=-2.58724 CenterZ=0 NormalX=0 NormalY=0 NormalZ=1 AngleXU=0 Radius=1
    g17: Circle CenterX=-6.32538 CenterY=-4 CenterZ=0 NormalX=0 NormalY=0 NormalZ=1 AngleXU=0 Radius=1
    g18: BSplineCurve PolesCount=3 KnotsCount=2 Degree=2 IsPeriodic=0
    g19: GeomPoint X=-6.2215 Y=-2 Z=0
    g20: GeomPoint X=-6.32538 Y=-4 Z=0
    g21: Circle CenterX=-6.48644 CenterY=-5.99526 CenterZ=0 NormalX=0 NormalY=0 NormalZ=1 AngleXU=0 Radius=1
    g22: Circle CenterX=-6.58486 CenterY=-6.99526 CenterZ=0 NormalX=0 NormalY=0 NormalZ=1 AngleXU=0 Radius=1
    g23: Circle CenterX=-6.77343 CenterY=-8 CenterZ=0 NormalX=0 NormalY=0 NormalZ=1 AngleXU=0 Radius=1
    g24: BSplineCurve PolesCount=3 KnotsCount=2 Degree=2 IsPeriodic=0
    g25: GeomPoint X=-6.48644 Y=-5.99526 Z=0
    g26: GeomPoint X=-6.77343 Y=-8 Z=0
    g27: Circle CenterX=-7.19003 CenterY=-10 CenterZ=0 NormalX=0 NormalY=0 NormalZ=1 AngleXU=0 Radius=1
    g28: Circle CenterX=-7.44407 CenterY=-11.0915 CenterZ=0 NormalX=0 NormalY=0 NormalZ=1 AngleXU=0 Radius=1
    g29: Circle CenterX=-7.79258 CenterY=-12 CenterZ=0 NormalX=0 NormalY=0 NormalZ=1 AngleXU=0 Radius=1
    g30: BSplineCurve PolesCount=3 KnotsCount=2 Degree=2 IsPeriodic=0
    g31: GeomPoint X=-7.19003 Y=-10 Z=0
    g32: GeomPoint X=-7.79258 Y=-12 Z=0
    g33: Circle CenterX=-8.70761 CenterY=-14 CenterZ=0 NormalX=0 NormalY=0 NormalZ=1 AngleXU=0 Radius=1
    g34: Circle CenterX=-9.33087 CenterY=-15.1837 CenterZ=0 NormalX=0 NormalY=0 NormalZ=1 AngleXU=0 Radius=1
    g35: Circle CenterX=-10.1571 CenterY=-16 CenterZ=0 NormalX=0 NormalY=0 NormalZ=1 AngleXU=0 Radius=1
    g36: BSplineCurve PolesCount=3 KnotsCount=2 Degree=2 IsPeriodic=0
    g37: GeomPoint X=-8.70761 Y=-14 Z=0
    g38: GeomPoint X=-10.1571 Y=-16 Z=0
    g39: Circle CenterX=-12.8401 CenterY=-17.6958 CenterZ=0 NormalX=0 NormalY=0 NormalZ=1 AngleXU=0 Radius=1
    g40: Circle CenterX=-13.3521 CenterY=-17.9027 CenterZ=0 NormalX=0 NormalY=0 NormalZ=1 AngleXU=0 Radius=1
    g41: Circle CenterX=-14 CenterY=-18 CenterZ=0 NormalX=0 NormalY=0 NormalZ=1 AngleXU=0 Radius=1
    g42: BSplineCurve PolesCount=3 KnotsCount=2 Degree=2 IsPeriodic=0
    g43: GeomPoint X=-12.8401 Y=-17.6958 Z=0
    g44: GeomPoint X=-14 Y=-18 Z=0
    g45: LineSegment StartX=-6.2 StartY=0 StartZ=0 EndX=-7.2 EndY=0 EndZ=0
    g46: LineSegment StartX=-7.2 StartY=0 StartZ=0 EndX=-7.2 EndY=-2 EndZ=0
    g47: LineSegment StartX=-7.2 StartY=-2 StartZ=0 EndX=-6.2215 EndY=-2 EndZ=0
    g48: LineSegment StartX=-6.32538 StartY=-4 StartZ=0 EndX=-7.65538 EndY=-4 EndZ=0
    g49: LineSegment StartX=-7.65538 StartY=-4 StartZ=0 EndX=-7.65538 EndY=-5.99526 EndZ=0
    g50: LineSegment StartX=-7.65538 StartY=-5.99526 StartZ=0 EndX=-6.48644 EndY=-5.99526 EndZ=0
    g51: LineSegment StartX=-6.77343 StartY=-8 StartZ=0 EndX=-8.43343 EndY=-8 EndZ=0
    g52: LineSegment StartX=-8.43343 StartY=-8 StartZ=0 EndX=-8.43343 EndY=-10 EndZ=0
    g53: LineSegment StartX=-8.43343 StartY=-10 StartZ=0 EndX=-7.19003 EndY=-10 EndZ=0
  constraints (112):
    c: Horizontal(g0)
    c: Distance(g0) = 2
    c: Block(g0)
    c: Vertical(g1)
    c: Coincident(g2,g0)
    c: Vertical(g2)
    c: Block(g2)
    c: Coincident(g6,g2)
    c: Weight(g3) = 1
    c: Equal(g3,g4)
    c: Equal(g3,g5)
    c: InternalAlignment(g3,g6)
    c: InternalAlignment(g4,g6)
    c: InternalAlignment(g5,g6)
    c: InternalAlignment(g7,g6)
    c: InternalAlignment(g8,g6)
    c: Block(g6)
    c: Coincident(g9,g1)
    c: Coincident(g9,g6)
    c: Horizontal(g9)
    c: Vertical(g10)
    c: Block(g10)
    c: Horizontal(g11)
    c: Block(g11)
    c: Coincident(g12,g10)
    c: Horizontal(g12)
    c: Block(g12)
    c: Coincident(g13,g11)
    c: Vertical(g13)
    c: Block(g13)
    c: Coincident(g14,g10)
    c: Horizontal(g14)
    c: Block(g14)
    c: Block(g9)
    c: Block(g1)
    c: Weight(g15) = 1
    c: Equal(g15,g16)
    c: Equal(g15,g17)
    c: InternalAlignment(g15,g18)
    c: InternalAlignment(g16,g18)
    c: InternalAlignment(g17,g18)
    c: InternalAlignment(g19,g18)
    c: InternalAlignment(g20,g18)
    c: Weight(g21) = 1
    c: Equal(g21,g22)
    c: Equal(g21,g23)
    c: InternalAlignment(g21,g24)
    c: InternalAlignment(g22,g24)
    c: InternalAlignment(g23,g24)
    c: InternalAlignment(g25,g24)
    c: InternalAlignment(g26,g24)
    c: Weight(g27) = 1
    c: Equal(g27,g28)
    c: Equal(g27,g29)
    c: Coincident(g30,g14)
    c: InternalAlignment(g27,g30)
    c: InternalAlignment(g28,g30)
    c: InternalAlignment(g29,g30)
    c: InternalAlignment(g31,g30)
    c: InternalAlignment(g32,g30)
    c: Coincident(g36,g12)
    c: Weight(g33) = 1
    c: Equal(g33,g34)
    c: Equal(g33,g35)
    c: Coincident(g36,g11)
    c: InternalAlignment(g33,g36)
    c: InternalAlignment(g34,g36)
    c: InternalAlignment(g35,g36)
    c: InternalAlignment(g37,g36)
    c: InternalAlignment(g38,g36)
    c: Coincident(g42,g13)
    c: Weight(g39) = 1
    c: Equal(g39,g40)
    c: Equal(g39,g41)
    c: Coincident(g42,g1)
    c: InternalAlignment(g39,g42)
    c: InternalAlignment(g40,g42)
    c: InternalAlignment(g41,g42)
    c: InternalAlignment(g43,g42)
    c: InternalAlignment(g44,g42)
    c: Block(g18)
    c: Block(g24)
    c: Block(g30)
    c: Block(g36)
    c: Block(g42)
    c: Horizontal(g45)
    c: Coincident(g45,g0)
    c: Vertical(g46)
    c: Coincident(g46,g45)
    c: Coincident(g47,g46)
    c: Coincident(g47,g18)
    c: Horizontal(g47)
    c: Block(g46)
    c: Coincident(g48,g18)
    c: Horizontal(g48)
    c: Distance(g48) = 1.33
    c: Vertical(g49)
    c: Coincident(g49,g48)
    c: Coincident(g50,g49)
    c: Coincident(g50,g24)
    c: Horizontal(g50)
    c: Tangent(g50,g22)
    c: Horizontal(g51)
    c: Coincident(g51,g24)
    c: Block(g51)
    c: Vertical(g52)
    c: Block(g52)
    c: Coincident(g52,g51)
    c: Coincident(g53,g52)
    c: Coincident(g53,g30)
    c: Horizontal(g53)
    c: Distance(g1) = 8.5
FEATURE [Part::Feature] Face024
  shape: bbox 9.8 x 26.5 x 2e-07 mm, 1 faces, 0 solids (baked)
FEATURE [Part::Revolution] Revolve024
  Angle = 360
  Axis = (0,1,0)
  Base = (0,0,0)
  FaceMakerClass = Part::FaceMakerBullseye
  Placement = pos=(0,0,0) rot=(0,0,1;1.5708rad)
  Solid = false
  Source = -> Face024
  Symmetric = false
FEATURE [Part::Feature] Face025
  shape: bbox 9.8 x 26.5 x 2e-07 mm, 1 faces, 0 solids (baked)
FEATURE [Part::Revolution] Revolve025
  Angle = 360
  Axis = (0,1,0)
  Base = (0,0,0)
  FaceMakerClass = Part::FaceMakerBullseye
  Placement = pos=(0,0,0) rot=(0,0,1;1.5708rad)
  Solid = false
  Source = -> Face025
  Symmetric = false
FEATURE [Part::MultiFuse] Fusion033
  Placement = pos=(-18,19,36) rot=(0,0,1;0rad)
  Shapes = -> [Revolve025,Revolve024]
FEATURE [Part::Cylinder] Cylinder014
  Angle = 360
  AttacherType = Attacher::AttachEngine3D
  Height = 20
  Placement = pos=(0,0,36.15) rot=(0,0,1;0rad)
  Radius = 14.3
FEATURE [Part::Cylinder] Cylinder015
  Angle = 360
  AttacherType = Attacher::AttachEngine3D
  Height = 10
  Placement = pos=(0,0,36.15) rot=(0,0,1;0rad)
  Radius = 4
FEATURE [Part::MultiFuse] Fusion034  label="removeToCreteHoleForPlugHousing004"
  Placement = pos=(-42,19,36) rot=(0,1,0;1.5708rad)
  Shapes = -> [Cylinder014,Cylinder015]
FEATURE [Part::Cut] Cut008  label="top004"
  Base = -> Cut004
  Placement = pos=(-1,0,0) rot=(0,0,1;0rad)
  Tool = -> Fusion034
FEATURE [Part::Box] Box005  label="Cube005"
  AttacherType = Attacher::AttachEngine3D
  Height = 28
  Length = 3
  Placement = pos=(110.7,19,22) rot=(0,0,1;0rad)
  Width = 15.7
FEATURE [Part::Cylinder] Cylinder016
  Angle = 360
  AttacherType = Attacher::AttachEngine3D
  Height = 10
  Placement = pos=(0,0,36.15) rot=(0,0,1;0rad)
  Radius = 4
FEATURE [Part::Cylinder] Cylinder017
  Angle = 360
  AttacherType = Attacher::AttachEngine3D
  Height = 20
  Placement = pos=(0,0,36.15) rot=(0,0,1;0rad)
  Radius = 10.3
FEATURE [Part::MultiFuse] Fusion035  label="removeToCreteHoleForPlugHousing005"
  Placement = pos=(70,19,36) rot=(0,1,0;1.5708rad)
  Shapes = -> [Cylinder017,Cylinder016]
FEATURE [Part::Cut] Cut009  label="plugHousingTab001"
  Base = -> Box005
  Placement = pos=(-107.4,-14,0) rot=(0,0,1;0rad)
  Tool = -> Fusion035
FEATURE [Part::Box] Box006  label="Cube006"
  AttacherType = Attacher::AttachEngine3D
  Height = 28
  Length = 3
  Placement = pos=(110.7,19,22) rot=(0,0,1;0rad)
  Width = 15.7
FEATURE [Part::Cylinder] Cylinder018
  Angle = 360
  AttacherType = Attacher::AttachEngine3D
  Height = 10
  Placement = pos=(0,0,36.15) rot=(0,0,1;0rad)
  Radius = 4
FEATURE [Part::Cylinder] Cylinder019
  Angle = 360
  AttacherType = Attacher::AttachEngine3D
  Height = 20
  Placement = pos=(0,0,36.15) rot=(0,0,1;0rad)
  Radius = 10.3
FEATURE [Part::MultiFuse] Fusion036  label="removeToCreteHoleForPlugHousing006"
  Placement = pos=(70,19,36) rot=(0,1,0;1.5708rad)
  Shapes = -> [Cylinder019,Cylinder018]
FEATURE [Part::Cut] Cut010  label="plugHousingTab002"
  Base = -> Box006
  Placement = pos=(-107.4,-14,0) rot=(0,0,1;0rad)
  Tool = -> Fusion036
FEATURE [Part::MultiFuse] Fusion037
  Placement = pos=(9.6,23,0) rot=(0,0,1;3.14159rad)
  Shapes = -> [Cut009,Cut010]
FEATURE [Part::Box] Box  label="Cube"
  AttacherType = Attacher::AttachEngine3D
  Height = 10
  Length = 3
  Placement = pos=(3.3,4,12) rot=(0,0,1;0rad)
  Width = 10
FEATURE [Part::Fillet] Fillet004
  Base = -> Fusion028
  Edges = 1 edges r=2: [Edge25]
FEATURE [Part::Fillet] Fillet005  label="plugHousing046"
  Base = -> Fillet004
  Edges = 1 edges r=2: [Edge8]
FEATURE [Part::Fillet] Fillet006
  Base = -> Box
  Edges = 1 edges r=2: [Edge11]
FEATURE [Part::Box] Box007  label="Cube007"
  AttacherType = Attacher::AttachEngine3D
  Height = 10
  Length = 3
  Placement = pos=(3.3,4,50) rot=(0,0,1;0rad)
  Width = 10
FEATURE [Part::Fillet] Fillet007
  Base = -> Box007
  Edges = 1 edges r=2: [Edge12]
FEATURE [Part::Box] Box008  label="Cube008"
  AttacherType = Attacher::AttachEngine3D
  Height = 28
  Length = 4
  Placement = pos=(5,0,22) rot=(0,0,1;0rad)
  Width = 10
FEATURE [Part::Fillet] Fillet008
  Base = -> Box008
  Edges = 1 edges r=1: [Edge7]
FEATURE [Part::Fillet] Fillet009
  Base = -> Fillet008
  Edges = 1 edges r=2: [Edge5]
FEATURE [Part::Fillet] Fillet010
  Base = -> Fillet009
  Edges = 1 edges r=2: [Edge2]
FEATURE [Sketcher::SketchObject] Sketch009  label="topSketch003"
  FullyConstrained = true
  sketch-geometry (4):
    g0: LineSegment StartX=16.8446 StartY=31.512 StartZ=0 EndX=16.3251 EndY=34.4666 EndZ=0
    g1: ArcOfCircle CenterX=19 CenterY=19.2524 CenterZ=0 NormalX=0 NormalY=0 NormalZ=1 AngleXU=0 Radius=15.4476 StartAngle=1.74483 EndAngle=2.72717
    g2: ArcOfCircle CenterX=19 CenterY=19.2524 CenterZ=0 NormalX=0 NormalY=0 NormalZ=1 AngleXU=0 Radius=12.4476 StartAngle=1.74483 EndAngle=2.73189
    g3: LineSegment StartX=4.86004 StartY=25.4725 StartZ=0 EndX=7.58253 EndY=24.2107 EndZ=0
  constraints (7):
    c: Block(g0)
    c: Coincident(g1,g0)
    c: Coincident(g2,g0)
    c: Coincident(g3,g1)
    c: Coincident(g3,g2)
    c: Block(g1)
    c: Block(g2)
FEATURE [Part::Extrusion] Extrude008
  Base = -> Sketch009
  Dir = (0,0,1)
  DirMode = 2
  FaceMakerClass = Part::FaceMakerBullseye
  LengthFwd = 10
  LengthRev = 0
  Placement = pos=(0,0,31) rot=(0,0,1;0rad)
  Solid = true
  Symmetric = false
FEATURE [Part::Cylinder] Cylinder020
  Angle = 360
  AttacherType = Attacher::AttachEngine3D
  Height = 20
  Placement = pos=(0,0,36.15) rot=(0,0,1;0rad)
  Radius = 8.2
FEATURE [Part::Cylinder] Cylinder021
  Angle = 360
  AttacherType = Attacher::AttachEngine3D
  Height = 10
  Placement = pos=(0,0,36.15) rot=(0,0,1;0rad)
  Radius = 4
FEATURE [Part::MultiFuse] Fusion038  label="removeToCreteHoleForPlugHousing007"
  Placement = pos=(-42,19,36) rot=(0,1,0;1.5708rad)
  Shapes = -> [Cylinder020,Cylinder021]
FEATURE [Part::Cut] Cut011
  Base = -> Extrude008
  Tool = -> Fusion038
FEATURE [Part::Fillet] Fillet011
  Base = -> Cut011
  Edges = 1 edges r=2: [Edge1]
FEATURE [Part::Fillet] Fillet012
  Base = -> Fillet011
  Edges = 1 edges r=2.5: [Edge1]
FEATURE [Part::Fillet] Fillet013
  Base = -> Fillet012
  Edges = 1 edges r=2.5: [Edge2]
FEATURE [Part::Box] Box010  label="Cube010"
  AttacherType = Attacher::AttachEngine3D
  Height = 16
  Length = 8
  Placement = pos=(12.7,31.52,28) rot=(0,0,1;0rad)
  Width = 4
FEATURE [Sketcher::SketchObject] Sketch010  label="topSketch004"
  FullyConstrained = true
  sketch-geometry (4):
    g0: LineSegment StartX=16.8446 StartY=31.512 StartZ=0 EndX=16.3251 EndY=34.4666 EndZ=0
    g1: ArcOfCircle CenterX=19 CenterY=19.2524 CenterZ=0 NormalX=0 NormalY=0 NormalZ=1 AngleXU=0 Radius=15.4476 StartAngle=1.74483 EndAngle=2.72717
    g2: ArcOfCircle CenterX=19 CenterY=19.2524 CenterZ=0 NormalX=0 NormalY=0 NormalZ=1 AngleXU=0 Radius=12.4476 StartAngle=1.74483 EndAngle=2.73189
    g3: LineSegment StartX=4.86004 StartY=25.4725 StartZ=0 EndX=7.58253 EndY=24.2107 EndZ=0
  constraints (7):
    c: Block(g0)
    c: Coincident(g1,g0)
    c: Coincident(g2,g0)
    c: Coincident(g3,g1)
    c: Coincident(g3,g2)
    c: Block(g1)
    c: Block(g2)
FEATURE [Part::Cylinder] Cylinder022
  Angle = 360
  AttacherType = Attacher::AttachEngine3D
  Height = 10
  Placement = pos=(0,0,36.15) rot=(0,0,1;0rad)
  Radius = 4
FEATURE [Sketcher::SketchObject] Sketch011  label="topSketch005"
  FullyConstrained = true
  sketch-geometry (4):
    g0: LineSegment StartX=16.8446 StartY=31.512 StartZ=0 EndX=16.3251 EndY=34.4666 EndZ=0
    g1: ArcOfCircle CenterX=19 CenterY=19.2524 CenterZ=0 NormalX=0 NormalY=0 NormalZ=1 AngleXU=0 Radius=15.4476 StartAngle=1.74483 EndAngle=2.72717
    g2: ArcOfCircle CenterX=19 CenterY=19.2524 CenterZ=0 NormalX=0 NormalY=0 NormalZ=1 AngleXU=0 Radius=12.4476 StartAngle=1.74483 EndAngle=2.73189
    g3: LineSegment StartX=4.86004 StartY=25.4725 StartZ=0 EndX=7.58253 EndY=24.2107 EndZ=0
  constraints (7):
    c: Block(g0)
    c: Coincident(g1,g0)
    c: Coincident(g2,g0)
    c: Coincident(g3,g1)
    c: Coincident(g3,g2)
    c: Block(g1)
    c: Block(g2)
FEATURE [Part::Extrusion] Extrude010
  Base = -> Sketch011
  Dir = (0,0,1)
  DirMode = 2
  FaceMakerClass = Part::FaceMakerBullseye
  LengthFwd = 10.6
  LengthRev = 0
  Placement = pos=(0,0,31) rot=(0,0,1;0rad)
  Solid = true
  Symmetric = false
FEATURE [Part::Cylinder] Cylinder023
  Angle = 360
  AttacherType = Attacher::AttachEngine3D
  Height = 20
  Placement = pos=(0,0,36.15) rot=(0,0,1;0rad)
  Radius = 8.2
FEATURE [Part::MultiFuse] Fusion039  label="removeToCreteHoleForPlugHousing008"
  Placement = pos=(-42,19,36) rot=(0,1,0;1.5708rad)
  Shapes = -> [Cylinder023,Cylinder022]
FEATURE [Part::Cut] Cut012
  Base = -> Extrude010
  Placement = pos=(0,0,-0.3) rot=(0,0,1;0rad)
  Tool = -> Fusion039
FEATURE [Part::Cut] Cut013
  Base = -> Box010
  Tool = -> Cut012
FEATURE [Part::Fillet] Fillet014
  Base = -> Cut013
  Edges = 1 edges r=0.7: [Edge13]
FEATURE [Part::Fillet] Fillet015
  Base = -> Fillet014
  Edges = 1 edges r=0.7: [Edge13]
FEATURE [Part::Fillet] Fillet016
  Base = -> Fillet015
  Edges = 1 edges r=0.7: [Edge16]
FEATURE [Part::Fillet] Fillet017
  Base = -> Fillet016
  Edges = 1 edges r=0.7: [Edge11]
FEATURE [Part::Fillet] Fillet018
  Base = -> Fillet017
  Edges = 1 edges r=0.7: [Edge10]
FEATURE [Part::Fillet] Fillet019
  Base = -> Fillet018
  Edges = 1 edges r=1.2: [Edge5]
FEATURE [Part::Fillet] Fillet020
  Base = -> Fillet019
  Edges = 1 edges r=1.2: [Edge12]
FEATURE [Part::Fillet] Fillet021
  Base = -> Fillet020
  Edges = 1 edges r=2: [Edge1]
  Placement = pos=(0.3,0,0) rot=(0,0,1;0rad)
FEATURE [Part::MultiFuse] Fusion040  label="top005"
  Shapes = -> [Cut008,Fillet021]
FEATURE [Part::MultiFuse] Fusion041  label="wireHolder"
  Shapes = -> [Fusion033,Fillet013]
FEATURE [Part::MultiFuse] Fusion042
  Shapes = -> [Fillet007,Fusion041]
FEATURE [Part::MultiFuse] Fusion043  label="wireHolder001"
  Shapes = -> [Fusion042,Fillet010]
FEATURE [Part::MultiFuse] Fusion044  label="wireHolder002"
  Shapes = -> [Fillet006,Fusion037,Fusion043]
FEATURE [Part::Feature] Face026
  shape: bbox 11 x 6 x 2e-07 mm, 1 faces, 0 solids (baked)
FEATURE [Part::Revolution] Revolve026
  Angle = 360
  Axis = (0,1,0)
  Base = (0,0,0)
  FaceMakerClass = Part::FaceMakerBullseye
  Placement = pos=(30.3,-1,19.7) rot=(0,0,1;0rad)
  Solid = false
  Source = -> Face026
  Symmetric = false
FEATURE [Sketcher::SketchObject] Sketch013  label="topSketch006"
  FullyConstrained = true
  sketch-geometry (13):
    g0: LineSegment StartX=117 StartY=19 StartZ=0 EndX=117 EndY=38 EndZ=0
    g1: ArcOfCircle CenterX=98 CenterY=19 CenterZ=0 NormalX=0 NormalY=0 NormalZ=1 AngleXU=0 Radius=19 StartAngle=5.7297 EndAngle=6.28319
    g2: LineSegment StartX=0 StartY=3 StartZ=0 EndX=0 EndY=19 EndZ=0
    g3: LineSegment StartX=19 StartY=38 StartZ=0 EndX=117 EndY=38 EndZ=0
    g4: ArcOfCircle CenterX=19 CenterY=19 CenterZ=0 NormalX=0 NormalY=0 NormalZ=1 AngleXU=0 Radius=19 StartAngle=1.5708 EndAngle=3.14159
    g5: ArcOfCircle CenterX=19 CenterY=19 CenterZ=0 NormalX=0 NormalY=0 NormalZ=1 AngleXU=0 Radius=16 StartAngle=1.5708 EndAngle=3.14159
    g6: ArcOfCircle CenterX=98 CenterY=19 CenterZ=0 NormalX=0 NormalY=0 NormalZ=1 AngleXU=0 Radius=16 StartAngle=5.60905 EndAngle=6.28319
    g7: LineSegment StartX=114 StartY=19 StartZ=0 EndX=114 EndY=35 EndZ=0
    g8: LineSegment StartX=110.5 StartY=9.01251 StartZ=0 EndX=114.163 EndY=9.01251 EndZ=0
    g9: LineSegment StartX=114 StartY=35 StartZ=0 EndX=19 EndY=35 EndZ=0
    g10: LineSegment StartX=0 StartY=3 StartZ=0 EndX=0 EndY=0 EndZ=0
    g11: LineSegment StartX=3 StartY=0 StartZ=0 EndX=0 EndY=0 EndZ=0
    g12: LineSegment StartX=3 StartY=19 StartZ=0 EndX=3 EndY=0 EndZ=0
  constraints (33):
    c: Vertical(g0)
    c: Distance(g0) = 19
    c: Block(g0)
    c: Coincident(g1,g0)
    c: Block(g1)
    c: Vertical(g2)
    c: Block(g2)
    c: Coincident(g3,g0)
    c: Horizontal(g3)
    c: Distance(g3) = 98
    c: Coincident(g4,g3)
    c: Coincident(g4,g2)
    c: Block(g4)
    c: Coincident(g5,g4)
    c: Coincident(g6,g1)
    c: Block(g6)
    c: Block(g5)
    c: Coincident(g7,g6)
    c: Vertical(g7)
    c: Coincident(g8,g6)
    c: Coincident(g8,g1)
    c: Coincident(g9,g7)
    c: Coincident(g9,g5)
    c: Horizontal(g9)
    c: Tangent(g9,g5)
    c: Coincident(g10,g2)
    c: Distance(g10) = 3
    c: Vertical(g10)
    c: Coincident(g11,g10)
    c: Horizontal(g11)
    c: Coincident(g12,g5)
    c: Coincident(g12,g11)
    c: Vertical(g12)
FEATURE [Part::Extrusion] Extrude011  label="top006"
  Base = -> Sketch013
  Dir = (0,0,1)
  DirMode = 2
  FaceMakerClass = Part::FaceMakerBullseye
  LengthFwd = 72
  LengthRev = 0
  Solid = true
  Symmetric = false
FEATURE [Sketcher::SketchObject] Sketch014
  FullyConstrained = true
  MapMode = 3
  Placement = pos=(0,0,0) rot=(1,0,0;1.5708rad)
  Support = -> [Extrude011]
  sketch-geometry (8):
    g0: Circle CenterX=80.351 CenterY=-67.6202 CenterZ=0 NormalX=0 NormalY=0 NormalZ=1 AngleXU=0 Radius=2
    g1: Circle CenterX=80.351 CenterY=-67.6202 CenterZ=0 NormalX=0 NormalY=0 NormalZ=1 AngleXU=0 Radius=3
    g2: Circle CenterX=80.351 CenterY=-4.92017 CenterZ=0 NormalX=0 NormalY=0 NormalZ=1 AngleXU=0 Radius=2
    g3: Circle CenterX=80.351 CenterY=-4.92017 CenterZ=0 NormalX=0 NormalY=0 NormalZ=1 AngleXU=0 Radius=3
    g4: Circle CenterX=23.851 CenterY=-4.92017 CenterZ=0 NormalX=0 NormalY=0 NormalZ=1 AngleXU=0 Radius=2
    g5: Circle CenterX=23.851 CenterY=-4.92017 CenterZ=0 NormalX=0 NormalY=0 NormalZ=1 AngleXU=0 Radius=3
    g6: Circle CenterX=23.851 CenterY=-67.6202 CenterZ=0 NormalX=0 NormalY=0 NormalZ=1 AngleXU=0 Radius=2
    g7: Circle CenterX=23.851 CenterY=-67.6202 CenterZ=0 NormalX=0 NormalY=0 NormalZ=1 AngleXU=0 Radius=3
  constraints (8):
    c: Block(g3)
    c: Block(g2)
    c: Block(g1)
    c: Block(g0)
    c: Block(g6)
    c: Block(g7)
    c: Block(g4)
    c: Block(g5)
FEATURE [Part::Feature] Face027
  shape: bbox 11 x 6 x 2e-07 mm, 1 faces, 0 solids (baked)
FEATURE [Part::Revolution] Revolve027
  Angle = 360
  Axis = (0,1,0)
  Base = (0,0,0)
  FaceMakerClass = Part::FaceMakerBullseye
  Placement = pos=(30.3,-1,51.7) rot=(0,0,1;0rad)
  Solid = false
  Source = -> Face027
  Symmetric = false
FEATURE [Part::Feature] Face028
  shape: bbox 11 x 6 x 2e-07 mm, 1 faces, 0 solids (baked)
FEATURE [Part::Revolution] Revolve028
  Angle = 360
  Axis = (0,1,0)
  Base = (0,0,0)
  FaceMakerClass = Part::FaceMakerBullseye
  Placement = pos=(62.3,-1,19.7) rot=(0,0,1;0rad)
  Solid = false
  Source = -> Face028
  Symmetric = false
FEATURE [Part::Feature] Face029
  shape: bbox 11 x 6 x 2e-07 mm, 1 faces, 0 solids (baked)
FEATURE [Part::Revolution] Revolve029
  Angle = 360
  Axis = (0,1,0)
  Base = (0,0,0)
  FaceMakerClass = Part::FaceMakerBullseye
  Placement = pos=(62.3,-1,51.7) rot=(0,0,1;0rad)
  Solid = false
  Source = -> Face029
  Symmetric = false
FEATURE [Part::Feature] Wire
  shape: bbox 11 x 5.2 x 2e-07 mm, 0 faces, 0 solids (baked)
FEATURE [Part::Revolution] Revolve030
  Angle = 360
  Axis = (0,1,0)
  Base = (0,0,0)
  FaceMakerClass = Part::FaceMakerBullseye
  Placement = pos=(30.3,38,19.7) rot=(0,0,1;0rad)
  Solid = true
  Source = -> Wire
  Symmetric = false
FEATURE [Part::Feature] Wire001
  shape: bbox 11 x 5.2 x 2e-07 mm, 0 faces, 0 solids (baked)
FEATURE [Part::Revolution] Revolve031
  Angle = 360
  Axis = (0,1,0)
  Base = (0,0,0)
  FaceMakerClass = Part::FaceMakerBullseye
  Placement = pos=(30.3,38,51.7) rot=(0,0,1;0rad)
  Solid = true
  Source = -> Wire001
  Symmetric = false
FEATURE [Part::Feature] Wire002
  shape: bbox 11 x 5.2 x 2e-07 mm, 0 faces, 0 solids (baked)
FEATURE [Part::Revolution] Revolve032
  Angle = 360
  Axis = (0,1,0)
  Base = (0,0,0)
  FaceMakerClass = Part::FaceMakerBullseye
  Placement = pos=(62.3,38,51.7) rot=(0,0,1;0rad)
  Solid = true
  Source = -> Wire002
  Symmetric = false
FEATURE [Part::Feature] Wire003
  shape: bbox 11 x 5.2 x 2e-07 mm, 0 faces, 0 solids (baked)
FEATURE [Part::Revolution] Revolve033
  Angle = 360
  Axis = (0,1,0)
  Base = (0,0,0)
  FaceMakerClass = Part::FaceMakerBullseye
  Placement = pos=(62.3,38,19.7) rot=(0,0,1;0rad)
  Solid = true
  Source = -> Wire003
  Symmetric = false
FEATURE [Part::MultiFuse] Fusion045  label="altRandScrewHousing"
  Shapes = -> [Revolve029,Revolve027,Revolve028,Revolve026]
FEATURE [Part::MultiFuse] Fusion046  label="fanScrewHousing"
  Shapes = -> [Revolve033,Revolve032,Revolve031,Revolve030]
FEATURE [Sketcher::SketchObject] Sketch015
  FullyConstrained = true
  sketch-geometry (17):
    g0: Circle CenterX=-3.5 CenterY=23.5 CenterZ=0 NormalX=0 NormalY=0 NormalZ=1 AngleXU=0 Radius=1
    g1: Circle CenterX=-1 CenterY=15.25 CenterZ=0 NormalX=0 NormalY=0 NormalZ=1 AngleXU=0 Radius=1
    g2: Circle CenterX=-3.5 CenterY=7 CenterZ=0 NormalX=0 NormalY=0 NormalZ=1 AngleXU=0 Radius=1
    g3: BSplineCurve PolesCount=3 KnotsCount=2 Degree=2 IsPeriodic=0
    g4: GeomPoint X=-3.5 Y=23.5 Z=0
    g5: GeomPoint X=-3.5 Y=7 Z=0
    g6: Circle CenterX=-4.8 CenterY=30.5 CenterZ=0 NormalX=0 NormalY=0 NormalZ=1 AngleXU=0 Radius=1
    g7: Circle CenterX=-3.5 CenterY=30.5 CenterZ=0 NormalX=0 NormalY=0 NormalZ=1 AngleXU=0 Radius=1
    g8: Circle CenterX=-3.5 CenterY=29.2 CenterZ=0 NormalX=0 NormalY=0 NormalZ=1 AngleXU=0 Radius=1
    g9: BSplineCurve PolesCount=3 KnotsCount=2 Degree=2 IsPeriodic=0
    g10: GeomPoint X=-4.8 Y=30.5 Z=0
    g11: GeomPoint X=-3.5 Y=29.2 Z=0
    g12: LineSegment StartX=-3.5 StartY=29.2 StartZ=0 EndX=-3.5 EndY=23.5 EndZ=0
    g13: LineSegment StartX=-4.8 StartY=30.5 StartZ=0 EndX=0 EndY=30.5 EndZ=0
    g14: LineSegment StartX=-3.5 StartY=0.3 StartZ=0 EndX=0 EndY=0.3 EndZ=0
    g15: LineSegment StartX=-3.5 StartY=0.3 StartZ=0 EndX=-3.5 EndY=7 EndZ=0
    g16: LineSegment StartX=0 StartY=0.3 StartZ=0 EndX=0 EndY=30.5 EndZ=0
  constraints (33):
    c: Weight(g0) = 1
    c: Equal(g0,g1)
    c: Equal(g0,g2)
    c: InternalAlignment(g0,g3)
    c: InternalAlignment(g1,g3)
    c: InternalAlignment(g2,g3)
    c: InternalAlignment(g4,g3)
    c: InternalAlignment(g5,g3)
    c: Block(g3)
    c: Weight(g6) = 1
    c: Equal(g6,g7)
    c: Equal(g6,g8)
    c: InternalAlignment(g6,g9)
    c: InternalAlignment(g7,g9)
    c: InternalAlignment(g8,g9)
    c: InternalAlignment(g10,g9)
    c: InternalAlignment(g11,g9)
    c: Block(g9)
    c: Coincident(g12,g9)
    c: Coincident(g12,g3)
    c: Vertical(g12)
    c: Coincident(g13,g9)
    c: Horizontal(g13)
    c: Distance(g13) = 4.8
    c: Horizontal(g14)
    c: Block(g14)
    c: Coincident(g15,g14)
    c: Coincident(g15,g3)
    c: Vertical(g15)
    c: Coincident(g16,g14)
    c: Coincident(g16,g13)
    c: Vertical(g16)
    c: Tangent(g16,g1)
FEATURE [Sketcher::SketchObject] Sketch016
  FullyConstrained = true
  sketch-geometry (16):
    g0: Circle CenterX=-3.5 CenterY=23.5 CenterZ=0 NormalX=0 NormalY=0 NormalZ=1 AngleXU=0 Radius=1
    g1: Circle CenterX=-1 CenterY=15.25 CenterZ=0 NormalX=0 NormalY=0 NormalZ=1 AngleXU=0 Radius=1
    g2: Circle CenterX=-3.5 CenterY=7 CenterZ=0 NormalX=0 NormalY=0 NormalZ=1 AngleXU=0 Radius=1
    g3: BSplineCurve PolesCount=3 KnotsCount=2 Degree=2 IsPeriodic=0
    g4: GeomPoint X=-3.5 Y=23.5 Z=0
    g5: GeomPoint X=-3.5 Y=7 Z=0
    g6: LineSegment StartX=-3.5 StartY=28.2 StartZ=0 EndX=-3.5 EndY=23.5 EndZ=0
    g7: LineSegment StartX=0 StartY=29.5 StartZ=0 EndX=0 EndY=30 EndZ=0
    g8: LineSegment StartX=-3.5 StartY=28.2 StartZ=0 EndX=-3.5 EndY=30 EndZ=0
    g9: LineSegment StartX=0 StartY=30 StartZ=0 EndX=0 EndY=30.5 EndZ=0
    g10: LineSegment StartX=0 StartY=30.5 StartZ=0 EndX=-3.5 EndY=30.5 EndZ=0
    g11: LineSegment StartX=-3.5 StartY=30.5 StartZ=0 EndX=-3.5 EndY=30 EndZ=0
    g12: LineSegment StartX=0 StartY=29.5 StartZ=0 EndX=0 EndY=5 EndZ=0
    g13: LineSegment StartX=-3.5 StartY=0.3 StartZ=0 EndX=-3.5 EndY=7 EndZ=0
    g14: LineSegment StartX=-3.5 StartY=0.3 StartZ=0 EndX=0 EndY=0.3 EndZ=0
    g15: LineSegment StartX=0 StartY=5 StartZ=0 EndX=0 EndY=0.3 EndZ=0
  constraints (39):
    c: Weight(g0) = 1
    c: Equal(g0,g1)
    c: Equal(g0,g2)
    c: InternalAlignment(g0,g3)
    c: InternalAlignment(g1,g3)
    c: InternalAlignment(g2,g3)
    c: InternalAlignment(g4,g3)
    c: InternalAlignment(g5,g3)
    c: Block(g3)
    c: Coincident(g6,g3)
    c: Vertical(g6)
    c: Vertical(g7)
    c: Distance(g7) = 0.5
    c: Coincident(g8,g6)
    c: Vertical(g8)
    c: Block(g6)
    c: Block(g7)
    c: Vertical(g9)
    c: Equal(g7,g9) = 0.5
    c: Block(g9)
    c: Coincident(g9,g7)
    c: Horizontal(g10)
    c: Coincident(g10,g9)
    c: Coincident(g11,g10)
    c: Coincident(g11,g8)
    c: Vertical(g11)
    c: Block(g11)
    c: Coincident(g12,g7)
    c: Vertical(g12)
    c: Coincident(g13,g3)
    c: Vertical(g13)
    c: Distance(g13) = 6.7
    c: Coincident(g14,g13)
    c: Horizontal(g14)
    c: Block(g14)
    c: Coincident(g15,g12)
    c: Coincident(g15,g14)
    c: Vertical(g15)
    c: Block(g15)
FEATURE [Sketcher::SketchObject] Sketch017
  FullyConstrained = true
  sketch-geometry (11):
    g0: LineSegment StartX=-3.5 StartY=1e-16 StartZ=0 EndX=-1.6 EndY=1e-16 EndZ=0
    g1: LineSegment StartX=-1.6 StartY=1e-16 StartZ=0 EndX=-1.6 EndY=1.5 EndZ=0
    g2: LineSegment StartX=-3.5 StartY=1.5 StartZ=0 EndX=-1.6 EndY=1.5 EndZ=0
    g3: LineSegment StartX=-3.5 StartY=1e-16 StartZ=0 EndX=-4.8 EndY=1e-16 EndZ=0
    g4: Circle CenterX=-3.5 CenterY=1.3 CenterZ=0 NormalX=0 NormalY=0 NormalZ=1 AngleXU=0 Radius=1
    g5: Circle CenterX=-3.5 CenterY=1e-16 CenterZ=0 NormalX=0 NormalY=0 NormalZ=1 AngleXU=0 Radius=1
    g6: Circle CenterX=-4.8 CenterY=1e-16 CenterZ=0 NormalX=0 NormalY=0 NormalZ=1 AngleXU=0 Radius=1
    g7: BSplineCurve PolesCount=3 KnotsCount=2 Degree=2 IsPeriodic=0
    g8: GeomPoint X=-3.5 Y=1.3 Z=0
    g9: GeomPoint X=-4.8 Y=1e-16 Z=0
    g10: LineSegment StartX=-3.5 StartY=1.3 StartZ=0 EndX=-3.5 EndY=1.5 EndZ=0
  constraints (24):
    c: Horizontal(g0)
    c: Distance(g0) = 1.9
    c: Block(g0)
    c: Coincident(g1,g0)
    c: Vertical(g1)
    c: Coincident(g2,g1)
    c: Horizontal(g2)
    c: Coincident(g3,g0)
    c: Horizontal(g3)
    c: Distance(g3) = 1.3
    c: Weight(g4) = 1
    c: Equal(g4,g5)
    c: Coincident(g5,g0)
    c: Equal(g4,g6)
    c: Coincident(g7,g3)
    c: InternalAlignment(g4,g7)
    c: InternalAlignment(g5,g7)
    c: InternalAlignment(g6,g7)
    c: InternalAlignment(g8,g7)
    c: InternalAlignment(g9,g7)
    c: Coincident(g10,g7)
    c: Coincident(g10,g2)
    c: Vertical(g10)
    c: Block(g10)
FEATURE [Part::Feature] Face035
  shape: bbox 3.2 x 1.5 x 2e-07 mm, 1 faces, 0 solids (baked)
FEATURE [Part::Revolution] Revolve039  label="backCaseScrewRetainer"
  Angle = 360
  Axis = (0,1,0)
  Base = (0,0,0)
  FaceMakerClass = Part::FaceMakerBullseye
  Placement = pos=(12.5,3,62) rot=(0,0,1;0rad)
  Solid = false
  Source = -> Face035
  Symmetric = false
FEATURE [Part::Feature] Face036
  shape: bbox 3.2 x 1.5 x 2e-07 mm, 1 faces, 0 solids (baked)
FEATURE [Part::Feature] Face039
  shape: bbox 4.8 x 30.2 x 2e-07 mm, 1 faces, 0 solids (baked)
FEATURE [Part::Revolution] Revolve043  label="frontCaseScrewPost002"
  Angle = 360
  Axis = (0,1,0)
  Base = (0,0,0)
  FaceMakerClass = Part::FaceMakerBullseye
  Placement = pos=(89.5,4.5,3.5) rot=(0,0,1;0rad)
  Solid = false
  Source = -> Face039
  Symmetric = false
FEATURE [Part::Feature] Face042
  shape: bbox 4.8 x 30.2 x 2e-07 mm, 1 faces, 0 solids (baked)
FEATURE [Part::Revolution] Revolve046  label="frontCaseScrewPost003"
  Angle = 360
  Axis = (0,1,0)
  Base = (0,0,0)
  FaceMakerClass = Part::FaceMakerBullseye
  Placement = pos=(89.5,4.5,68.5) rot=(0,0,1;0rad)
  Solid = false
  Source = -> Face042
  Symmetric = false
FEATURE [Part::Feature] Face043
  shape: bbox 3.2 x 1.5 x 2e-07 mm, 1 faces, 0 solids (baked)
FEATURE [Part::Revolution] Revolve047  label="frontCaseScrewRetainer002"
  Angle = 360
  Axis = (0,1,0)
  Base = (0,0,0)
  FaceMakerClass = Part::FaceMakerBullseye
  Placement = pos=(89.5,3,68.5) rot=(0,0,1;0rad)
  Solid = false
  Source = -> Face043
  Symmetric = false
FEATURE [Part::Feature] Face044
  shape: bbox 3.2 x 1.5 x 2e-07 mm, 1 faces, 0 solids (baked)
FEATURE [Part::Revolution] Revolve048  label="frontCaseScrewRetainer003"
  Angle = 360
  Axis = (0,1,0)
  Base = (0,0,0)
  FaceMakerClass = Part::FaceMakerBullseye
  Placement = pos=(89.5,3,3.5) rot=(0,0,1;0rad)
  Solid = false
  Source = -> Face044
  Symmetric = false
FEATURE [App::MeasureDistance] Distance002  label="Distance: 1.67 mm"
  Distance = 1.66921
  P1 = (99.2361,4.7524,71.7)
  P2 = (99.2347,6.42161,71.7)
FEATURE [Sketcher::SketchObject] Sketch018
  FullyConstrained = true
  sketch-geometry (7):
    g0: LineSegment StartX=0 StartY=0 StartZ=0 EndX=0 EndY=6 EndZ=0
    g1: Circle CenterX=0 CenterY=0 CenterZ=0 NormalX=0 NormalY=0 NormalZ=1 AngleXU=0 Radius=1
    g2: Circle CenterX=8 CenterY=6 CenterZ=0 NormalX=0 NormalY=0 NormalZ=1 AngleXU=0 Radius=1
    g3: BSplineCurve PolesCount=3 KnotsCount=2 Degree=2 IsPeriodic=0
    g4: GeomPoint X=0 Y=0 Z=0
    g5: GeomPoint X=8 Y=6 Z=0
    g6: LineSegment StartX=0 StartY=6 StartZ=0 EndX=8 EndY=6 EndZ=0
  constraints (14):
    c: Coincident(g0,g-1)
    c: Distance(g0) = 6
    c: Vertical(g0)
    c: Coincident(g3,g0)
    c: Weight(g1) = 1
    c: Equal(g1,g2)
    c: InternalAlignment(g1,g3)
    c: InternalAlignment(g2,g3)
    c: InternalAlignment(g4,g3)
    c: InternalAlignment(g5,g3)
    c: Block(g3)
    c: Coincident(g6,g0)
    c: Coincident(g6,g3)
    c: Horizontal(g6)
FEATURE [Part::Extrusion] Extrude012  label="caseScrewPillarBracket"
  Base = -> Sketch018
  Dir = (0,0,1)
  DirMode = 2
  FaceMakerClass = Part::FaceMakerBullseye
  LengthFwd = 2.4
  LengthRev = 0
  Placement = pos=(15.76,29,8.8) rot=(0,1,0;0rad)
  Solid = true
  Symmetric = false
FEATURE [Sketcher::SketchObject] Sketch019
  FullyConstrained = true
  sketch-geometry (7):
    g0: LineSegment StartX=0 StartY=0 StartZ=0 EndX=0 EndY=6 EndZ=0
    g1: Circle CenterX=0 CenterY=0 CenterZ=0 NormalX=0 NormalY=0 NormalZ=1 AngleXU=0 Radius=1
    g2: Circle CenterX=8 CenterY=6 CenterZ=0 NormalX=0 NormalY=0 NormalZ=1 AngleXU=0 Radius=1
    g3: BSplineCurve PolesCount=3 KnotsCount=2 Degree=2 IsPeriodic=0
    g4: GeomPoint X=0 Y=0 Z=0
    g5: GeomPoint X=8 Y=6 Z=0
    g6: LineSegment StartX=0 StartY=6 StartZ=0 EndX=8 EndY=6 EndZ=0
  constraints (14):
    c: Coincident(g0,g-1)
    c: Distance(g0) = 6
    c: Vertical(g0)
    c: Coincident(g3,g0)
    c: Weight(g1) = 1
    c: Equal(g1,g2)
    c: InternalAlignment(g1,g3)
    c: InternalAlignment(g2,g3)
    c: InternalAlignment(g4,g3)
    c: InternalAlignment(g5,g3)
    c: Block(g3)
    c: Coincident(g6,g0)
    c: Coincident(g6,g3)
    c: Horizontal(g6)
FEATURE [Part::Extrusion] Extrude013  label="caseScrewPillarBracket001"
  Base = -> Sketch019
  Dir = (0,0,1)
  DirMode = 2
  FaceMakerClass = Part::FaceMakerBullseye
  LengthFwd = 2.4
  LengthRev = 0
  Placement = pos=(15.76,29,60.8) rot=(0,0,1;0rad)
  Solid = true
  Symmetric = false
FEATURE [Sketcher::SketchObject] Sketch020
  FullyConstrained = true
  sketch-geometry (7):
    g0: LineSegment StartX=0 StartY=0 StartZ=0 EndX=0 EndY=6 EndZ=0
    g1: Circle CenterX=0 CenterY=0 CenterZ=0 NormalX=0 NormalY=0 NormalZ=1 AngleXU=0 Radius=1
    g2: Circle CenterX=8 CenterY=6 CenterZ=0 NormalX=0 NormalY=0 NormalZ=1 AngleXU=0 Radius=1
    g3: BSplineCurve PolesCount=3 KnotsCount=2 Degree=2 IsPeriodic=0
    g4: GeomPoint X=0 Y=0 Z=0
    g5: GeomPoint X=8 Y=6 Z=0
    g6: LineSegment StartX=0 StartY=6 StartZ=0 EndX=8 EndY=6 EndZ=0
  constraints (14):
    c: Coincident(g0,g-1)
    c: Distance(g0) = 6
    c: Vertical(g0)
    c: Coincident(g3,g0)
    c: Weight(g1) = 1
    c: Equal(g1,g2)
    c: InternalAlignment(g1,g3)
    c: InternalAlignment(g2,g3)
    c: InternalAlignment(g4,g3)
    c: InternalAlignment(g5,g3)
    c: Block(g3)
    c: Coincident(g6,g0)
    c: Coincident(g6,g3)
    c: Horizontal(g6)
FEATURE [Part::Extrusion] Extrude014  label="caseScrewPillarBracket002"
  Base = -> Sketch020
  Dir = (0,0,1)
  DirMode = 2
  FaceMakerClass = Part::FaceMakerBullseye
  LengthFwd = 2.4
  LengthRev = 0
  Placement = pos=(13.7,29,13.26) rot=(0,1,0;-1.5708rad)
  Solid = true
  Symmetric = false
FEATURE [Sketcher::SketchObject] Sketch021
  FullyConstrained = true
  sketch-geometry (7):
    g0: LineSegment StartX=0 StartY=0 StartZ=0 EndX=0 EndY=6 EndZ=0
    g1: Circle CenterX=0 CenterY=0 CenterZ=0 NormalX=0 NormalY=0 NormalZ=1 AngleXU=0 Radius=1
    g2: Circle CenterX=8 CenterY=6 CenterZ=0 NormalX=0 NormalY=0 NormalZ=1 AngleXU=0 Radius=1
    g3: BSplineCurve PolesCount=3 KnotsCount=2 Degree=2 IsPeriodic=0
    g4: GeomPoint X=0 Y=0 Z=0
    g5: GeomPoint X=8 Y=6 Z=0
    g6: LineSegment StartX=0 StartY=6 StartZ=0 EndX=8 EndY=6 EndZ=0
  constraints (14):
    c: Coincident(g0,g-1)
    c: Distance(g0) = 6
    c: Vertical(g0)
    c: Coincident(g3,g0)
    c: Weight(g1) = 1
    c: Equal(g1,g2)
    c: InternalAlignment(g1,g3)
    c: InternalAlignment(g2,g3)
    c: InternalAlignment(g4,g3)
    c: InternalAlignment(g5,g3)
    c: Block(g3)
    c: Coincident(g6,g0)
    c: Coincident(g6,g3)
    c: Horizontal(g6)
FEATURE [Part::Extrusion] Extrude015  label="caseScrewPillarBracket003"
  Base = -> Sketch021
  Dir = (0,0,1)
  DirMode = 2
  FaceMakerClass = Part::FaceMakerBullseye
  LengthFwd = 2.4
  LengthRev = 0
  Placement = pos=(11.3,29,58.74) rot=(0,1,0;1.5708rad)
  Solid = true
  Symmetric = false
FEATURE [Sketcher::SketchObject] Sketch022
  FullyConstrained = true
  sketch-geometry (7):
    g0: LineSegment StartX=0 StartY=0 StartZ=0 EndX=0 EndY=6 EndZ=0
    g1: Circle CenterX=0 CenterY=0 CenterZ=0 NormalX=0 NormalY=0 NormalZ=1 AngleXU=0 Radius=1
    g2: Circle CenterX=8 CenterY=6 CenterZ=0 NormalX=0 NormalY=0 NormalZ=1 AngleXU=0 Radius=1
    g3: BSplineCurve PolesCount=3 KnotsCount=2 Degree=2 IsPeriodic=0
    g4: GeomPoint X=0 Y=0 Z=0
    g5: GeomPoint X=8 Y=6 Z=0
    g6: LineSegment StartX=0 StartY=6 StartZ=0 EndX=8 EndY=6 EndZ=0
  constraints (14):
    c: Coincident(g0,g-1)
    c: Distance(g0) = 6
    c: Vertical(g0)
    c: Coincident(g3,g0)
    c: Weight(g1) = 1
    c: Equal(g1,g2)
    c: InternalAlignment(g1,g3)
    c: InternalAlignment(g2,g3)
    c: InternalAlignment(g4,g3)
    c: InternalAlignment(g5,g3)
    c: Block(g3)
    c: Coincident(g6,g0)
    c: Coincident(g6,g3)
    c: Horizontal(g6)
FEATURE [Part::Extrusion] Extrude016  label="caseScrewPillarBracket004"
  Base = -> Sketch022
  Dir = (0,0,1)
  DirMode = 2
  FaceMakerClass = Part::FaceMakerBullseye
  LengthFwd = 2.4
  LengthRev = 0
  Placement = pos=(88.3,29,65.23) rot=(0,1,0;1.5708rad)
  Solid = true
  Symmetric = false
FEATURE [Sketcher::SketchObject] Sketch023
  FullyConstrained = true
  sketch-geometry (7):
    g0: LineSegment StartX=0 StartY=0 StartZ=0 EndX=0 EndY=6 EndZ=0
    g1: Circle CenterX=0 CenterY=0 CenterZ=0 NormalX=0 NormalY=0 NormalZ=1 AngleXU=0 Radius=1
    g2: Circle CenterX=8 CenterY=6 CenterZ=0 NormalX=0 NormalY=0 NormalZ=1 AngleXU=0 Radius=1
    g3: BSplineCurve PolesCount=3 KnotsCount=2 Degree=2 IsPeriodic=0
    g4: GeomPoint X=0 Y=0 Z=0
    g5: GeomPoint X=8 Y=6 Z=0
    g6: LineSegment StartX=0 StartY=6 StartZ=0 EndX=8 EndY=6 EndZ=0
  constraints (14):
    c: Coincident(g0,g-1)
    c: Distance(g0) = 6
    c: Vertical(g0)
    c: Coincident(g3,g0)
    c: Weight(g1) = 1
    c: Equal(g1,g2)
    c: InternalAlignment(g1,g3)
    c: InternalAlignment(g2,g3)
    c: InternalAlignment(g4,g3)
    c: InternalAlignment(g5,g3)
    c: Block(g3)
    c: Coincident(g6,g0)
    c: Coincident(g6,g3)
    c: Horizontal(g6)
FEATURE [Part::Extrusion] Extrude017  label="caseScrewPillarBracket005"
  Base = -> Sketch023
  Dir = (0,0,1)
  DirMode = 2
  FaceMakerClass = Part::FaceMakerBullseye
  LengthFwd = 2.4
  LengthRev = 0
  Placement = pos=(90.7,29,6.77) rot=(0,-1,0;1.5708rad)
  Solid = true
  Symmetric = false
FEATURE [Sketcher::SketchObject] Sketch024
  FullyConstrained = true
  sketch-geometry (7):
    g0: LineSegment StartX=0 StartY=0 StartZ=0 EndX=0 EndY=6 EndZ=0
    g1: Circle CenterX=0 CenterY=0 CenterZ=0 NormalX=0 NormalY=0 NormalZ=1 AngleXU=0 Radius=1
    g2: Circle CenterX=8 CenterY=6 CenterZ=0 NormalX=0 NormalY=0 NormalZ=1 AngleXU=0 Radius=1
    g3: BSplineCurve PolesCount=3 KnotsCount=2 Degree=2 IsPeriodic=0
    g4: GeomPoint X=0 Y=0 Z=0
    g5: GeomPoint X=8 Y=6 Z=0
    g6: LineSegment StartX=0 StartY=6 StartZ=0 EndX=8 EndY=6 EndZ=0
  constraints (14):
    c: Coincident(g0,g-1)
    c: Distance(g0) = 6
    c: Vertical(g0)
    c: Coincident(g3,g0)
    c: Weight(g1) = 1
    c: Equal(g1,g2)
    c: InternalAlignment(g1,g3)
    c: InternalAlignment(g2,g3)
    c: InternalAlignment(g4,g3)
    c: InternalAlignment(g5,g3)
    c: Block(g3)
    c: Coincident(g6,g0)
    c: Coincident(g6,g3)
    c: Horizontal(g6)
FEATURE [Part::Extrusion] Extrude018  label="caseScrewPillarBracket006"
  Base = -> Sketch024
  Dir = (0,0,1)
  DirMode = 2
  FaceMakerClass = Part::FaceMakerBullseye
  LengthFwd = 2.4
  LengthRev = 0
  Placement = pos=(103.7,29,6.77) rot=(0,-1,0;1.5708rad)
  Solid = true
  Symmetric = false
FEATURE [Sketcher::SketchObject] Sketch025
  FullyConstrained = true
  sketch-geometry (7):
    g0: LineSegment StartX=0 StartY=0 StartZ=0 EndX=0 EndY=6 EndZ=0
    g1: Circle CenterX=0 CenterY=0 CenterZ=0 NormalX=0 NormalY=0 NormalZ=1 AngleXU=0 Radius=1
    g2: Circle CenterX=8 CenterY=6 CenterZ=0 NormalX=0 NormalY=0 NormalZ=1 AngleXU=0 Radius=1
    g3: BSplineCurve PolesCount=3 KnotsCount=2 Degree=2 IsPeriodic=0
    g4: GeomPoint X=0 Y=0 Z=0
    g5: GeomPoint X=8 Y=6 Z=0
    g6: LineSegment StartX=0 StartY=6 StartZ=0 EndX=8 EndY=6 EndZ=0
  constraints (14):
    c: Coincident(g0,g-1)
    c: Distance(g0) = 6
    c: Vertical(g0)
    c: Coincident(g3,g0)
    c: Weight(g1) = 1
    c: Equal(g1,g2)
    c: InternalAlignment(g1,g3)
    c: InternalAlignment(g2,g3)
    c: InternalAlignment(g4,g3)
    c: InternalAlignment(g5,g3)
    c: Block(g3)
    c: Coincident(g6,g0)
    c: Coincident(g6,g3)
    c: Horizontal(g6)
FEATURE [Part::Extrusion] Extrude019  label="caseScrewPillarBracket007"
  Base = -> Sketch025
  Dir = (0,0,1)
  DirMode = 2
  FaceMakerClass = Part::FaceMakerBullseye
  LengthFwd = 2.4
  LengthRev = 0
  Placement = pos=(101.3,29,65.23) rot=(0,1,0;1.5708rad)
  Solid = true
  Symmetric = false
FEATURE [Part::Box] Box011  label="frontCaseScrewPillarBracket"
  AttacherType = Attacher::AttachEngine3D
  Height = 2.4
  Length = 16
  Placement = pos=(87,28,2.3) rot=(0,0,1;0rad)
  Width = 7
FEATURE [Part::Box] Box012  label="frontCaseScrewPillarBracket001"
  AttacherType = Attacher::AttachEngine3D
  Height = 2.4
  Length = 16
  Placement = pos=(87,28,67.3) rot=(0,0,1;0rad)
  Width = 7
FEATURE [Sketcher::SketchObject] Sketch026
  FullyConstrained = true
  sketch-geometry (17):
    g0: Circle CenterX=-3.5 CenterY=23.5 CenterZ=0 NormalX=0 NormalY=0 NormalZ=1 AngleXU=0 Radius=1
    g1: Circle CenterX=-1 CenterY=15.25 CenterZ=0 NormalX=0 NormalY=0 NormalZ=1 AngleXU=0 Radius=1
    g2: Circle CenterX=-3.5 CenterY=7 CenterZ=0 NormalX=0 NormalY=0 NormalZ=1 AngleXU=0 Radius=1
    g3: BSplineCurve PolesCount=3 KnotsCount=2 Degree=2 IsPeriodic=0
    g4: GeomPoint X=-3.5 Y=23.5 Z=0
    g5: GeomPoint X=-3.5 Y=7 Z=0
    g6: Circle CenterX=-4.8 CenterY=30.5 CenterZ=0 NormalX=0 NormalY=0 NormalZ=1 AngleXU=0 Radius=1
    g7: Circle CenterX=-3.5 CenterY=30.5 CenterZ=0 NormalX=0 NormalY=0 NormalZ=1 AngleXU=0 Radius=1
    g8: Circle CenterX=-3.5 CenterY=29.2 CenterZ=0 NormalX=0 NormalY=0 NormalZ=1 AngleXU=0 Radius=1
    g9: BSplineCurve PolesCount=3 KnotsCount=2 Degree=2 IsPeriodic=0
    g10: GeomPoint X=-4.8 Y=30.5 Z=0
    g11: GeomPoint X=-3.5 Y=29.2 Z=0
    g12: LineSegment StartX=-3.5 StartY=29.2 StartZ=0 EndX=-3.5 EndY=23.5 EndZ=0
    g13: LineSegment StartX=-4.8 StartY=30.5 StartZ=0 EndX=0 EndY=30.5 EndZ=0
    g14: LineSegment StartX=-3.5 StartY=5 StartZ=0 EndX=-3.5 EndY=7 EndZ=0
    g15: LineSegment StartX=0 StartY=5 StartZ=0 EndX=0 EndY=30.5 EndZ=0
    g16: LineSegment StartX=-3.5 StartY=5 StartZ=0 EndX=0 EndY=5 EndZ=0
  constraints (33):
    c: Weight(g0) = 1
    c: Equal(g0,g1)
    c: Equal(g0,g2)
    c: InternalAlignment(g0,g3)
    c: InternalAlignment(g1,g3)
    c: InternalAlignment(g2,g3)
    c: InternalAlignment(g4,g3)
    c: InternalAlignment(g5,g3)
    c: Block(g3)
    c: Weight(g6) = 1
    c: Equal(g6,g7)
    c: Equal(g6,g8)
    c: InternalAlignment(g6,g9)
    c: InternalAlignment(g7,g9)
    c: InternalAlignment(g8,g9)
    c: InternalAlignment(g10,g9)
    c: InternalAlignment(g11,g9)
    c: Block(g9)
    c: Coincident(g12,g9)
    c: Coincident(g12,g3)
    c: Vertical(g12)
    c: Coincident(g13,g9)
    c: Horizontal(g13)
    c: Distance(g13) = 4.8
    c: Coincident(g14,g3)
    c: Vertical(g14)
    c: Coincident(g15,g13)
    c: Vertical(g15)
    c: Tangent(g15,g1)
    c: Distance(g14) = 2
    c: Coincident(g16,g14)
    c: Horizontal(g16)
    c: Coincident(g15,g16)
FEATURE [Part::Feature] Face050
  shape: bbox 4.8 x 25.5 x 2e-07 mm, 1 faces, 0 solids (baked)
FEATURE [Part::Revolution] Revolve054  label="moreFrontCaseScrewPost001"
  Angle = 360
  Axis = (0,1,0)
  Base = (0,0,0)
  FaceMakerClass = Part::FaceMakerBullseye
  Placement = pos=(102.5,4.5,3.5) rot=(0,0,1;0rad)
  Solid = false
  Source = -> Face050
  Symmetric = false
FEATURE [Part::Feature] Face051
  shape: bbox 4.8 x 25.5 x 2e-07 mm, 1 faces, 0 solids (baked)
FEATURE [Part::Revolution] Revolve055  label="moreFrontCaseScrewPost002"
  Angle = 360
  Axis = (0,1,0)
  Base = (0,0,0)
  FaceMakerClass = Part::FaceMakerBullseye
  Placement = pos=(102.5,4.5,68.5) rot=(0,0,1;0rad)
  Solid = false
  Source = -> Face051
  Symmetric = false
FEATURE [Sketcher::SketchObject] Sketch027
  FullyConstrained = true
  sketch-geometry (10):
    g0: LineSegment StartX=-1.6 StartY=4.7 StartZ=0 EndX=-1.6 EndY=1.7 EndZ=0
    g1: LineSegment StartX=-3.5 StartY=4.7 StartZ=0 EndX=-1.6 EndY=4.7 EndZ=0
    g2: LineSegment StartX=-1.6 StartY=1.7 StartZ=0 EndX=-1.6 EndY=1.5 EndZ=0
    g3: LineSegment StartX=-1.6 StartY=1.5 StartZ=0 EndX=-5.2 EndY=1.5 EndZ=0
    g4: Circle CenterX=-3.5 CenterY=4.7 CenterZ=0 NormalX=0 NormalY=0 NormalZ=1 AngleXU=0 Radius=1
    g5: Circle CenterX=-3.59627 CenterY=2.99743 CenterZ=0 NormalX=0 NormalY=0 NormalZ=1 AngleXU=0 Radius=1
    g6: Circle CenterX=-5.2 CenterY=1.5 CenterZ=0 NormalX=0 NormalY=0 NormalZ=1 AngleXU=0 Radius=1
    g7: BSplineCurve PolesCount=3 KnotsCount=2 Degree=2 IsPeriodic=0
    g8: GeomPoint X=-3.5 Y=4.7 Z=0
    g9: GeomPoint X=-5.2 Y=1.5 Z=0
  constraints (23):
    c: Vertical(g0)
    c: Distance(g0) = 3
    c: Coincident(g1,g0)
    c: Horizontal(g1)
    c: Block(g0)
    c: Block(g1)
    c: Coincident(g2,g0)
    c: Vertical(g2)
    c: Distance(g2) = 0.2
    c: Coincident(g3,g2)
    c: Horizontal(g3)
    c: Block(g3)
    c: Coincident(g7,g1)
    c: Weight(g4) = 1
    c: Equal(g4,g5)
    c: Equal(g4,g6)
    c: Coincident(g7,g3)
    c: InternalAlignment(g4,g7)
    c: InternalAlignment(g5,g7)
    c: InternalAlignment(g6,g7)
    c: InternalAlignment(g8,g7)
    c: InternalAlignment(g9,g7)
    c: Block(g7)
FEATURE [Sketcher::SketchObject] Sketch028
  FullyConstrained = true
  sketch-geometry (18):
    g0: LineSegment StartX=0 StartY=3e-16 StartZ=0 EndX=0 EndY=1.7 EndZ=0
    g1: LineSegment StartX=-3.5 StartY=0 StartZ=0 EndX=-3.5 EndY=0.9 EndZ=0
    g2: Circle CenterX=-2.7 CenterY=1.7 CenterZ=0 NormalX=0 NormalY=0 NormalZ=1 AngleXU=0 Radius=1
    g3: Circle CenterX=-3.5 CenterY=1.7 CenterZ=0 NormalX=0 NormalY=0 NormalZ=1 AngleXU=0 Radius=1
    g4: Circle CenterX=-3.5 CenterY=0.9 CenterZ=0 NormalX=0 NormalY=0 NormalZ=1 AngleXU=0 Radius=1
    g5: BSplineCurve PolesCount=3 KnotsCount=2 Degree=2 IsPeriodic=0
    g6: GeomPoint X=-2.7 Y=1.7 Z=0
    g7: GeomPoint X=-3.5 Y=0.9 Z=0
    g8: LineSegment StartX=-3.5 StartY=0 StartZ=0 EndX=-3.5 EndY=-7 EndZ=0
    g9: LineSegment StartX=0 StartY=3e-16 StartZ=0 EndX=0 EndY=-7 EndZ=0
    g10: LineSegment StartX=-3.5 StartY=-7 StartZ=0 EndX=0 EndY=-7 EndZ=0
    g11: LineSegment StartX=-2.7 StartY=1.7 StartZ=0 EndX=-1.6 EndY=1.7 EndZ=0
    g12: LineSegment StartX=0 StartY=1.7 StartZ=0 EndX=0 EndY=4.5 EndZ=0
    g13: LineSegment StartX=0 StartY=4.5 StartZ=0 EndX=0 EndY=10.8 EndZ=0
    g14: LineSegment StartX=0 StartY=10.8 StartZ=0 EndX=-2 EndY=10.8 EndZ=0
    g15: LineSegment StartX=-1.6 StartY=4.7 StartZ=0 EndX=-1.6 EndY=1.7 EndZ=0
    g16: LineSegment StartX=-1.6 StartY=4.7 StartZ=0 EndX=-2 EndY=4.7 EndZ=0
    g17: LineSegment StartX=-2 StartY=4.7 StartZ=0 EndX=-2 EndY=10.8 EndZ=0
  constraints (44):
    c: Vertical(g0)
    c: Vertical(g1)
    c: Distance(g1) = 0.9
    c: Block(g0)
    c: Distance(g0) = 1.7
    c: Weight(g2) = 1
    c: Equal(g2,g3)
    c: Equal(g2,g4)
    c: Coincident(g5,g1)
    c: InternalAlignment(g2,g5)
    c: InternalAlignment(g3,g5)
    c: InternalAlignment(g4,g5)
    c: InternalAlignment(g6,g5)
    c: InternalAlignment(g7,g5)
    c: Block(g5)
    c: Coincident(g8,g1)
    c: Vertical(g8)
    c: Distance(g8) = 7
    c: Vertical(g9)
    c: Equal(g8,g9) = 7
    c: Coincident(g9,g0)
    c: Coincident(g10,g8)
    c: Coincident(g10,g9)
    c: Horizontal(g10)
    c: Coincident(g11,g5)
    c: Horizontal(g11)
    c: Coincident(g12,g0)
    c: Vertical(g12)
    c: Distance(g12) = 2.8
    c: Coincident(g13,g12)
    c: Vertical(g13)
    c: Distance(g13) = 6.3
    c: Coincident(g14,g13)
    c: Horizontal(g14)
    c: Distance(g14) = 2
    c: Vertical(g15)
    c: Distance(g15) = 3
    c: Block(g11)
    c: Coincident(g15,g11)
    c: Coincident(g16,g15)
    c: Horizontal(g16)
    c: Coincident(g17,g16)
    c: Coincident(g17,g14)
    c: Vertical(g17)
FEATURE [Part::Revolution] Revolve040  label="backCaseScrewRetainer001"
  Angle = 360
  Axis = (0,1,0)
  Base = (0,0,0)
  FaceMakerClass = Part::FaceMakerBullseye
  Placement = pos=(12.5,3,10) rot=(0,0,1;0rad)
  Solid = false
  Source = -> Face036
  Symmetric = false
FEATURE [Part::Feature] Face055
  shape: bbox 3.5 x 30.2 x 2e-07 mm, 1 faces, 0 solids (baked)
FEATURE [Part::Revolution] Revolve059  label="backCaseScrewPost"
  Angle = 360
  Axis = (0,1,0)
  Base = (0,0,0)
  FaceMakerClass = Part::FaceMakerBullseye
  Placement = pos=(12.5,4.5,10) rot=(0,0,1;0rad)
  Solid = false
  Source = -> Face055
  Symmetric = false
FEATURE [Part::Feature] Face056
  shape: bbox 3.5 x 30.2 x 2e-07 mm, 1 faces, 0 solids (baked)
FEATURE [Part::Revolution] Revolve060  label="backCaseScrewPost001"
  Angle = 360
  Axis = (0,1,0)
  Base = (0,0,0)
  FaceMakerClass = Part::FaceMakerBullseye
  Placement = pos=(12.5,4.5,62) rot=(0,0,1;0rad)
  Solid = false
  Source = -> Face056
  Symmetric = false
FEATURE [Part::Feature] Face057
  shape: bbox 3.5 x 17.8 x 2e-07 mm, 1 faces, 0 solids (baked)
FEATURE [Part::Revolution] Revolve061  label="removeToCreateScrewAndThreadedInsertHole"
  Angle = 360
  Axis = (0,1,0)
  Base = (0,0,0)
  FaceMakerClass = Part::FaceMakerBullseye
  Placement = pos=(12.5,0,10) rot=(0,0,1;0rad)
  Solid = false
  Source = -> Face057
  Symmetric = false
FEATURE [Part::Feature] Face058
  shape: bbox 3.5 x 17.8 x 2e-07 mm, 1 faces, 0 solids (baked)
FEATURE [Part::Revolution] Revolve062  label="removeToCreateScrewAndThreadedInsertHole001"
  Angle = 360
  Axis = (0,1,0)
  Base = (0,0,0)
  FaceMakerClass = Part::FaceMakerBullseye
  Placement = pos=(12.5,0,62) rot=(0,0,1;0rad)
  Solid = false
  Source = -> Face058
  Symmetric = false
FEATURE [Part::Feature] Face059
  shape: bbox 3.5 x 17.8 x 2e-07 mm, 1 faces, 0 solids (baked)
FEATURE [Part::Revolution] Revolve063  label="removeToCreateScrewAndThreadedInsertHole002"
  Angle = 360
  Axis = (0,1,0)
  Base = (0,0,0)
  FaceMakerClass = Part::FaceMakerBullseye
  Placement = pos=(89.5,0,68.5) rot=(0,0,1;0rad)
  Solid = false
  Source = -> Face059
  Symmetric = false
FEATURE [Part::Feature] Face060
  shape: bbox 3.5 x 17.8 x 2e-07 mm, 1 faces, 0 solids (baked)
FEATURE [Part::Revolution] Revolve064  label="removeToCreateScrewAndThreadedInsertHole003"
  Angle = 360
  Axis = (0,1,0)
  Base = (0,0,0)
  FaceMakerClass = Part::FaceMakerBullseye
  Placement = pos=(89.5,0,3.5) rot=(0,0,1;0rad)
  Solid = false
  Source = -> Face060
  Symmetric = false
FEATURE [Part::Feature] Face061
  shape: bbox 3.5 x 17.8 x 2e-07 mm, 1 faces, 0 solids (baked)
FEATURE [Part::Revolution] Revolve065  label="removeToCreateScrewAndThreadedInsertHole004"
  Angle = 360
  Axis = (0,1,0)
  Base = (0,0,0)
  FaceMakerClass = Part::FaceMakerBullseye
  Placement = pos=(102.5,4.7,3.5) rot=(0,0,1;0rad)
  Solid = false
  Source = -> Face061
  Symmetric = false
FEATURE [Part::Feature] Face062
  shape: bbox 3.5 x 17.8 x 2e-07 mm, 1 faces, 0 solids (baked)
FEATURE [Part::Revolution] Revolve066  label="removeToCreateScrewAndThreadedInsertHole005"
  Angle = 360
  Axis = (0,1,0)
  Base = (0,0,0)
  FaceMakerClass = Part::FaceMakerBullseye
  Placement = pos=(102.5,4.7,68.5) rot=(0,0,1;0rad)
  Solid = false
  Source = -> Face062
  Symmetric = false
FEATURE [Part::MultiFuse] Fusion047  label="makeHoles"
  Shapes = -> [Revolve066,Revolve065,Revolve064,Revolve063,Revolve062,Revolve061]
FEATURE [Part::Feature] Face063
  shape: bbox 3.6 x 3.2 x 2e-07 mm, 1 faces, 0 solids (baked)
FEATURE [Part::Revolution] Revolve067  label="moreFrontCaseScrewRetainer002"
  Angle = 360
  Axis = (0,1,0)
  Base = (0,0,0)
  FaceMakerClass = Part::FaceMakerBullseye
  Placement = pos=(102.5,4.5,68.5) rot=(0,0,1;0rad)
  Solid = false
  Source = -> Face063
  Symmetric = false
FEATURE [Part::Feature] Face064
  shape: bbox 3.6 x 3.2 x 2e-07 mm, 1 faces, 0 solids (baked)
FEATURE [Part::Revolution] Revolve068  label="moreFrontCaseScrewRetainer003"
  Angle = 360
  Axis = (0,1,0)
  Base = (0,0,0)
  FaceMakerClass = Part::FaceMakerBullseye
  Placement = pos=(102.5,4.5,3.5) rot=(0,0,1;0rad)
  Solid = false
  Source = -> Face064
  Symmetric = false
FEATURE [Part::Cut] Cut014  label="bottom003"
  Base = -> Cut007
  Tool = -> Fusion047
FEATURE [Part::Feature] Face065
  shape: bbox 3.5 x 17.8 x 2e-07 mm, 1 faces, 0 solids (baked)
FEATURE [Part::Revolution] Revolve069  label="removeToCreateScrewAndThreadedInsertHole006"
  Angle = 360
  Axis = (0,1,0)
  Base = (0,0,0)
  FaceMakerClass = Part::FaceMakerBullseye
  Placement = pos=(12.5,0,10) rot=(0,0,1;0rad)
  Solid = false
  Source = -> Face065
  Symmetric = false
FEATURE [Part::Feature] Face066
  shape: bbox 3.5 x 17.8 x 2e-07 mm, 1 faces, 0 solids (baked)
FEATURE [Part::Revolution] Revolve070  label="removeToCreateScrewAndThreadedInsertHole007"
  Angle = 360
  Axis = (0,1,0)
  Base = (0,0,0)
  FaceMakerClass = Part::FaceMakerBullseye
  Placement = pos=(12.5,0,62) rot=(0,0,1;0rad)
  Solid = false
  Source = -> Face066
  Symmetric = false
FEATURE [Part::Feature] Face067
  shape: bbox 3.5 x 17.8 x 2e-07 mm, 1 faces, 0 solids (baked)
FEATURE [Part::Revolution] Revolve071  label="removeToCreateScrewAndThreadedInsertHole008"
  Angle = 360
  Axis = (0,1,0)
  Base = (0,0,0)
  FaceMakerClass = Part::FaceMakerBullseye
  Placement = pos=(89.5,0,68.5) rot=(0,0,1;0rad)
  Solid = false
  Source = -> Face067
  Symmetric = false
FEATURE [Part::Feature] Face068
  shape: bbox 3.5 x 17.8 x 2e-07 mm, 1 faces, 0 solids (baked)
FEATURE [Part::Revolution] Revolve072  label="removeToCreateScrewAndThreadedInsertHole009"
  Angle = 360
  Axis = (0,1,0)
  Base = (0,0,0)
  FaceMakerClass = Part::FaceMakerBullseye
  Placement = pos=(89.5,0,3.5) rot=(0,0,1;0rad)
  Solid = false
  Source = -> Face068
  Symmetric = false
FEATURE [Part::Feature] Face069
  shape: bbox 3.5 x 17.8 x 2e-07 mm, 1 faces, 0 solids (baked)
FEATURE [Part::Feature] Face070
  shape: bbox 3.5 x 17.8 x 2e-07 mm, 1 faces, 0 solids (baked)
FEATURE [Part::Revolution] Revolve073  label="removeToCreateScrewAndThreadedInsertHole010"
  Angle = 360
  Axis = (0,1,0)
  Base = (0,0,0)
  FaceMakerClass = Part::FaceMakerBullseye
  Placement = pos=(102.5,4.7,3.5) rot=(0,0,1;0rad)
  Solid = false
  Source = -> Face069
  Symmetric = false
FEATURE [Part::Revolution] Revolve074  label="removeToCreateScrewAndThreadedInsertHole011"
  Angle = 360
  Axis = (0,1,0)
  Base = (0,0,0)
  FaceMakerClass = Part::FaceMakerBullseye
  Placement = pos=(102.5,4.7,68.5) rot=(0,0,1;0rad)
  Solid = false
  Source = -> Face070
  Symmetric = false
FEATURE [Part::MultiFuse] Fusion048  label="makeHoles001"
  Shapes = -> [Revolve074,Revolve073,Revolve072,Revolve071,Revolve070,Revolve069]
FEATURE [Part::MultiFuse] Fusion049  label="caseScrewRetainers"
  Shapes = -> [Revolve067,Revolve068,Revolve048,Revolve047,Revolve039,Revolve040]
FEATURE [Part::Cut] Cut015  label="caseScrewRetainers001"
  Base = -> Fusion049
  Tool = -> Fusion048
FEATURE [Part::MultiFuse] Fusion050  label="casePillars"
  Shapes = -> [Revolve055,Revolve054,Revolve043,Revolve046,Revolve059,Revolve060]
FEATURE [Part::Feature] Face071 .. Face076  x6 (patterned run collapsed; names and placements below)
  shape: bbox 3.5 x 17.8 x 2e-07 mm, 1 faces, 0 solids (baked)
FEATURE [Part::Revolution] Revolve075  label="removeToCreateScrewAndThreadedInsertHole012"
  Angle = 360
  Axis = (0,1,0)
  Base = (0,0,0)
  FaceMakerClass = Part::FaceMakerBullseye
  Placement = pos=(12.5,0,10) rot=(0,0,1;0rad)
  Solid = false
  Source = -> Face071
  Symmetric = false
FEATURE [Part::Revolution] Revolve076  label="removeToCreateScrewAndThreadedInsertHole013"
  Angle = 360
  Axis = (0,1,0)
  Base = (0,0,0)
  FaceMakerClass = Part::FaceMakerBullseye
  Placement = pos=(12.5,0,62) rot=(0,0,1;0rad)
  Solid = false
  Source = -> Face072
  Symmetric = false
FEATURE [Part::Revolution] Revolve077  label="removeToCreateScrewAndThreadedInsertHole014"
  Angle = 360
  Axis = (0,1,0)
  Base = (0,0,0)
  FaceMakerClass = Part::FaceMakerBullseye
  Placement = pos=(89.5,0,68.5) rot=(0,0,1;0rad)
  Solid = false
  Source = -> Face073
  Symmetric = false
FEATURE [Part::Revolution] Revolve078  label="removeToCreateScrewAndThreadedInsertHole015"
  Angle = 360
  Axis = (0,1,0)
  Base = (0,0,0)
  FaceMakerClass = Part::FaceMakerBullseye
  Placement = pos=(89.5,0,3.5) rot=(0,0,1;0rad)
  Solid = false
  Source = -> Face074
  Symmetric = false
FEATURE [Part::Revolution] Revolve079  label="removeToCreateScrewAndThreadedInsertHole016"
  Angle = 360
  Axis = (0,1,0)
  Base = (0,0,0)
  FaceMakerClass = Part::FaceMakerBullseye
  Placement = pos=(102.5,4.7,3.5) rot=(0,0,1;0rad)
  Solid = false
  Source = -> Face075
  Symmetric = false
FEATURE [Part::Revolution] Revolve080  label="removeToCreateScrewAndThreadedInsertHole017"
  Angle = 360
  Axis = (0,1,0)
  Base = (0,0,0)
  FaceMakerClass = Part::FaceMakerBullseye
  Placement = pos=(102.5,4.7,68.5) rot=(0,0,1;0rad)
  Solid = false
  Source = -> Face076
  Symmetric = false
FEATURE [Part::MultiFuse] Fusion051  label="makeHoles002"
  Shapes = -> [Revolve080,Revolve079,Revolve078,Revolve077,Revolve076,Revolve075]
FEATURE [Part::Cut] Cut016  label="caesPillars"
  Base = -> Fusion050
  Tool = -> Fusion051
FEATURE [Part::Revolution] Revolve009  label="plugHousing016"
  Angle = 360
  Axis = (0,1,0)
  Base = (0,0,0)
  FaceMakerClass = Part::FaceMakerBullseye
  Placement = pos=(0,0,36.15) rot=(0,0,1;0rad)
  Solid = false
  Source = -> Face012
  Symmetric = false
FEATURE [Part::MultiFuse] Fusion014  label="plugHousing023"
  Placement = pos=(0,0,0) rot=(0,0,1;1.5708rad)
  Shapes = -> [Revolve011,Revolve009]
FEATURE [Part::Revolution] Revolve010  label="plugHousing017"
  Angle = 360
  Axis = (0,1,0)
  Base = (0,0,0)
  FaceMakerClass = Part::FaceMakerBullseye
  Placement = pos=(0,0,36.15) rot=(0,0,1;0rad)
  Solid = false
  Source = -> Face014
  Symmetric = false
FEATURE [Part::MultiFuse] Fusion015  label="plugHousing024"
  Placement = pos=(0,0,0) rot=(0,0,1;1.5708rad)
  Shapes = -> [Revolve010,Revolve015]
FEATURE [Part::Revolution] Revolve014  label="plugHousing026"
  Angle = 360
  Axis = (0,1,0)
  Base = (0,0,0)
  FaceMakerClass = Part::FaceMakerBullseye
  Placement = pos=(0,0,36.15) rot=(0,0,1;0rad)
  Solid = false
  Source = -> Face011
  Symmetric = false
FEATURE [Part::Revolution] Revolve013  label="plugHousing025"
  Angle = 360
  Axis = (0,1,0)
  Base = (0,0,0)
  FaceMakerClass = Part::FaceMakerBullseye
  Placement = pos=(0,0,36.15) rot=(0,0,1;0rad)
  Solid = false
  Source = -> Face015
  Symmetric = false
FEATURE [Part::MultiFuse] Fusion016  label="plugHousing028"
  Placement = pos=(0,19,0) rot=(0,0,1;3.14159rad)
  Shapes = -> [Fusion014,Fusion013]
FEATURE [Part::MultiFuse] Fusion011  label="plugHousing018"
  Placement = pos=(0,0,0) rot=(0,0,1;1.5708rad)
  Shapes = -> [Revolve014,Revolve013]
FEATURE [Part::MultiFuse] Fusion012  label="plugHousing019"
  Placement = pos=(0,19,0) rot=(0,0,1;3.14159rad)
  Shapes = -> [Fusion011,Fusion015]
FEATURE [Part::MultiFuse] Fusion017  label="plugHousing029"
  Placement = pos=(122.621,0,-0.15) rot=(0,0,1;0rad)
  Shapes = -> [Fusion016,Fusion012]
FEATURE [Part::MultiFuse] Fusion052  label="casePillarRetainers"
  Shapes = -> [Extrude012,Extrude013,Extrude014,Extrude015,Extrude016,Extrude017,Extrude018,Extrude019,Box011,Box012]
FEATURE [Part::Feature] Face077
  shape: bbox 3.5 x 17.8 x 2e-07 mm, 1 faces, 0 solids (baked)
FEATURE [Part::Revolution] Revolve081  label="removeToCreateScrewAndThreadedInsertHole018"
  Angle = 360
  Axis = (0,1,0)
  Base = (0,0,0)
  FaceMakerClass = Part::FaceMakerBullseye
  Placement = pos=(62.3,30.3,19.7) rot=(0,0,1;0rad)
  Solid = false
  Source = -> Face077
  Symmetric = false
FEATURE [Part::Feature] Face078
  shape: bbox 3.5 x 17.8 x 2e-07 mm, 1 faces, 0 solids (baked)
FEATURE [Part::Revolution] Revolve082  label="removeToCreateScrewAndThreadedInsertHole019"
  Angle = 360
  Axis = (0,1,0)
  Base = (0,0,0)
  FaceMakerClass = Part::FaceMakerBullseye
  Placement = pos=(62.3,30.3,51.7) rot=(0,0,1;0rad)
  Solid = false
  Source = -> Face078
  Symmetric = false
FEATURE [Part::Feature] Face079
  shape: bbox 3.5 x 17.8 x 2e-07 mm, 1 faces, 0 solids (baked)
FEATURE [Part::Revolution] Revolve083  label="removeToCreateScrewAndThreadedInsertHole020"
  Angle = 360
  Axis = (0,1,0)
  Base = (0,0,0)
  FaceMakerClass = Part::FaceMakerBullseye
  Placement = pos=(30.3,30.3,19.7) rot=(0,0,1;0rad)
  Solid = false
  Source = -> Face079
  Symmetric = false
FEATURE [Part::Feature] Face080
  shape: bbox 3.5 x 17.8 x 2e-07 mm, 1 faces, 0 solids (baked)
FEATURE [Part::Revolution] Revolve084  label="removeToCreateScrewAndThreadedInsertHole021"
  Angle = 360
  Axis = (0,1,0)
  Base = (0,0,0)
  FaceMakerClass = Part::FaceMakerBullseye
  Placement = pos=(30.3,30.3,51.7) rot=(0,0,1;0rad)
  Solid = false
  Source = -> Face080
  Symmetric = false
FEATURE [Part::MultiFuse] Fusion053  label="createThreadedInsertHolesForFan"
  Shapes = -> [Revolve081,Revolve082,Revolve083,Revolve084]
FEATURE [Part::Cut] Cut017  label="fanScrewHousing001"
  Base = -> Fusion046
  Tool = -> Fusion053
FEATURE [Part::Feature] Face081
  shape: bbox 3.5 x 17.8 x 2e-07 mm, 1 faces, 0 solids (baked)
FEATURE [Part::Revolution] Revolve085  label="removeToCreateScrewAndThreadedInsertHole022"
  Angle = 360
  Axis = (0,1,0)
  Base = (0,0,0)
  FaceMakerClass = Part::FaceMakerBullseye
  Placement = pos=(62.3,30.3,19.7) rot=(0,0,1;0rad)
  Solid = false
  Source = -> Face081
  Symmetric = false
FEATURE [Part::Feature] Face082
  shape: bbox 3.5 x 17.8 x 2e-07 mm, 1 faces, 0 solids (baked)
FEATURE [Part::Revolution] Revolve086  label="removeToCreateScrewAndThreadedInsertHole023"
  Angle = 360
  Axis = (0,1,0)
  Base = (0,0,0)
  FaceMakerClass = Part::FaceMakerBullseye
  Placement = pos=(62.3,30.3,51.7) rot=(0,0,1;0rad)
  Solid = false
  Source = -> Face082
  Symmetric = false
FEATURE [Part::Feature] Face083
  shape: bbox 3.5 x 17.8 x 2e-07 mm, 1 faces, 0 solids (baked)
FEATURE [Part::Revolution] Revolve087  label="removeToCreateScrewAndThreadedInsertHole024"
  Angle = 360
  Axis = (0,1,0)
  Base = (0,0,0)
  FaceMakerClass = Part::FaceMakerBullseye
  Placement = pos=(30.3,30.3,19.7) rot=(0,0,1;0rad)
  Solid = false
  Source = -> Face083
  Symmetric = false
FEATURE [Part::Feature] Face084
  shape: bbox 3.5 x 17.8 x 2e-07 mm, 1 faces, 0 solids (baked)
FEATURE [Part::Revolution] Revolve088  label="removeToCreateScrewAndThreadedInsertHole025"
  Angle = 360
  Axis = (0,1,0)
  Base = (0,0,0)
  FaceMakerClass = Part::FaceMakerBullseye
  Placement = pos=(30.3,30.3,51.7) rot=(0,0,1;0rad)
  Solid = false
  Source = -> Face084
  Symmetric = false
FEATURE [Part::MultiFuse] Fusion054  label="createThreadedInsertHolesForFan001"
  Shapes = -> [Revolve085,Revolve086,Revolve087,Revolve088]
FEATURE [Part::Cut] Cut018  label="top007"
  Base = -> Fusion040
  Tool = -> Fusion054
FEATURE [Sketcher::SketchObject] Sketch029
  FullyConstrained = false
  Placement = pos=(0,0,0) rot=(1,0,0;1.5708rad)
  sketch-geometry (24):
    g0: ArcOfCircle CenterX=-4 CenterY=-10.5 CenterZ=0 NormalX=0 NormalY=0 NormalZ=1 AngleXU=0 Radius=1.5 StartAngle=6e-16 EndAngle=3.14159
    g1: ArcOfCircle CenterX=-34.2 CenterY=-10.5 CenterZ=0 NormalX=0 NormalY=0 NormalZ=1 AngleXU=0 Radius=1.5 StartAngle=0 EndAngle=3.14159
    g2: ArcOfCircle CenterX=-34.2 CenterY=-27.7 CenterZ=0 NormalX=0 NormalY=0 NormalZ=1 AngleXU=0 Radius=1.5 StartAngle=3.14159 EndAngle=6.28319
    g3: ArcOfCircle CenterX=-4 CenterY=-27.7 CenterZ=0 NormalX=0 NormalY=0 NormalZ=1 AngleXU=0 Radius=1.5 StartAngle=3.1416 EndAngle=6.28319
    g4: ArcOfCircle CenterX=-10 CenterY=-4.3 CenterZ=0 NormalX=0 NormalY=0 NormalZ=1 AngleXU=0 Radius=1.5 StartAngle=2e-16 EndAngle=3.14159
    g5: ArcOfCircle CenterX=-16.1 CenterY=-1.8 CenterZ=0 NormalX=0 NormalY=0 NormalZ=1 AngleXU=0 Radius=1.5 StartAngle=5e-16 EndAngle=3.14159
    g6: ArcOfCircle CenterX=-22.1 CenterY=-1.8 CenterZ=0 NormalX=0 NormalY=0 NormalZ=1 AngleXU=0 Radius=1.5 StartAngle=5e-16 EndAngle=3.14159
    g7: ArcOfCircle CenterX=-28.2 CenterY=-4.3 CenterZ=0 NormalX=0 NormalY=0 NormalZ=1 AngleXU=0 Radius=1.5 StartAngle=2e-16 EndAngle=3.14159
    g8: ArcOfCircle CenterX=-10 CenterY=-33.9 CenterZ=0 NormalX=0 NormalY=0 NormalZ=1 AngleXU=0 Radius=1.5 StartAngle=3.14159 EndAngle=6.28319
    g9: ArcOfCircle CenterX=-16.1 CenterY=-36.4 CenterZ=0 NormalX=0 NormalY=0 NormalZ=1 AngleXU=0 Radius=1.5 StartAngle=3.14159 EndAngle=6.28319
    g10: ArcOfCircle CenterX=-22.1 CenterY=-36.4 CenterZ=0 NormalX=0 NormalY=0 NormalZ=1 AngleXU=0 Radius=1.5 StartAngle=3.14159 EndAngle=6.28319
    g11: ArcOfCircle CenterX=-28.2 CenterY=-33.9 CenterZ=0 NormalX=0 NormalY=0 NormalZ=1 AngleXU=0 Radius=1.5 StartAngle=3.14159 EndAngle=6.28319
    g12: LineSegment StartX=-35.7 StartY=-10.5 StartZ=0 EndX=-35.7 EndY=-27.7 EndZ=0
    g13: LineSegment StartX=-32.7 StartY=-10.5 StartZ=0 EndX=-32.7 EndY=-27.7 EndZ=0
    g14: LineSegment StartX=-29.7 StartY=-33.9 StartZ=0 EndX=-29.7 EndY=-4.3 EndZ=0
    g15: LineSegment StartX=-26.7 StartY=-33.9 StartZ=0 EndX=-26.7 EndY=-4.3 EndZ=0
    g16: LineSegment StartX=-2.5 StartY=-10.5 StartZ=0 EndX=-2.5 EndY=-27.7 EndZ=0
    g17: LineSegment StartX=-8.5 StartY=-4.3 StartZ=0 EndX=-8.5 EndY=-33.9 EndZ=0
    g18: LineSegment StartX=-5.5 StartY=-10.5 StartZ=0 EndX=-5.5 EndY=-27.7 EndZ=0
    g19: LineSegment StartX=-11.5 StartY=-4.3 StartZ=0 EndX=-11.5 EndY=-33.9 EndZ=0
    g20: LineSegment StartX=-14.6 StartY=-1.8 StartZ=0 EndX=-14.6 EndY=-36.4 EndZ=0
    g21: LineSegment StartX=-17.6 StartY=-1.8 StartZ=0 EndX=-17.6 EndY=-36.4 EndZ=0
    g22: LineSegment StartX=-20.6 StartY=-36.4 StartZ=0 EndX=-20.6 EndY=-1.8 EndZ=0
    g23: LineSegment StartX=-23.6 StartY=-1.8 StartZ=0 EndX=-23.6 EndY=-36.4 EndZ=0
  constraints (48):
    c: Block(g0)
    c: Block(g1)
    c: Block(g2)
    c: Block(g3)
    c: Block(g4)
    c: Block(g5)
    c: Block(g6)
    c: Block(g7)
    c: Block(g8)
    c: Block(g9)
    c: Block(g10)
    c: Block(g11)
    c: Coincident(g12,g1)
    c: Coincident(g12,g2)
    c: Vertical(g12)
    c: Coincident(g13,g1)
    c: Coincident(g13,g2)
    c: Vertical(g13)
    c: Coincident(g14,g11)
    c: Coincident(g14,g7)
    c: Vertical(g14)
    c: Coincident(g15,g11)
    c: Coincident(g15,g7)
    c: Vertical(g15)
    c: Coincident(g16,g0)
    c: Coincident(g16,g3)
    c: Vertical(g16)
    c: Coincident(g17,g4)
    c: Coincident(g17,g8)
    c: Vertical(g17)
    c: Coincident(g18,g0)
    c: Coincident(g18,g3)
    c: Vertical(g18)
    c: Coincident(g19,g4)
    c: Coincident(g19,g8)
    c: Vertical(g19)
    c: Coincident(g20,g5)
    c: Coincident(g20,g9)
    c: Vertical(g20)
    c: Coincident(g21,g5)
    c: Coincident(g21,g9)
    c: Vertical(g21)
    c: Coincident(g22,g10)
    c: Coincident(g22,g6)
    c: Vertical(g22)
    c: Coincident(g23,g6)
    c: Coincident(g23,g10)
    c: Vertical(g23)
FEATURE [Part::Extrusion] Extrude020  label="removeToCreateFanGrillHoles"
  Base = -> Sketch029
  Dir = (0,-1,6e-16)
  DirMode = 2
  FaceMakerClass = Part::FaceMakerBullseye
  LengthFwd = 10
  LengthRev = 0
  Placement = pos=(65.4,44,54.82) rot=(0,0,1;0rad)
  Solid = true
  Symmetric = false
FEATURE [Part::MultiFuse] Fusion055  label="top008"
  Shapes = -> [Cut017,Cut018]
FEATURE [Part::Cut] Cut019  label="top009"
  Base = -> Fusion055
  Tool = -> Extrude020
FEATURE [App::MeasureDistance] Distance003  label="Distance: 71.95 mm"
  Distance = 71.9513
  P1 = (117,38,72)
  P2 = (117,38,0.0487319)
FEATURE [Sketcher::SketchObject] Sketch030
  FullyConstrained = true
  Placement = pos=(117,19,0) rot=(0.57735,0.57735,0.57735;2.0944rad)
  sketch-geometry (48):
    g0: LineSegment StartX=-49.19 StartY=69.25 StartZ=0 EndX=-49.19 EndY=66.25 EndZ=0
    g1: LineSegment StartX=-49.19 StartY=63.5 StartZ=0 EndX=-49.19 EndY=60.5 EndZ=0
    g2: LineSegment StartX=-49.19 StartY=57.75 StartZ=0 EndX=-49.19 EndY=54.75 EndZ=0
    g3: LineSegment StartX=-49.19 StartY=52 StartZ=0 EndX=-49.19 EndY=49 EndZ=0
    g4: LineSegment StartX=-49.19 StartY=46.25 StartZ=0 EndX=-49.19 EndY=43.25 EndZ=0
    g5: LineSegment StartX=-49.19 StartY=40.5 StartZ=0 EndX=-49.19 EndY=37.5 EndZ=0
    g6: LineSegment StartX=-49.19 StartY=34.5 StartZ=0 EndX=-49.19 EndY=31.5 EndZ=0
    g7: LineSegment StartX=-49.19 StartY=28.75 StartZ=0 EndX=-49.19 EndY=25.75 EndZ=0
    g8: LineSegment StartX=-49.19 StartY=23 StartZ=0 EndX=-49.19 EndY=20 EndZ=0
    g9: LineSegment StartX=-49.19 StartY=17.25 StartZ=0 EndX=-49.19 EndY=14.25 EndZ=0
    g10: LineSegment StartX=-49.19 StartY=11.5 StartZ=0 EndX=-49.19 EndY=8.5 EndZ=0
    g11: LineSegment StartX=-49.19 StartY=5.75 StartZ=0 EndX=-49.19 EndY=2.75 EndZ=0
    g12: ArcOfCircle CenterX=-1.5 CenterY=67.75 CenterZ=0 NormalX=0 NormalY=0 NormalZ=1 AngleXU=0 Radius=1.5 StartAngle=4.71239 EndAngle=7.85398
    g13: ArcOfCircle CenterX=-1.5 CenterY=62 CenterZ=0 NormalX=0 NormalY=0 NormalZ=1 AngleXU=0 Radius=1.5 StartAngle=4.71239 EndAngle=7.85398
    g14: ArcOfCircle CenterX=-1.5 CenterY=56.25 CenterZ=0 NormalX=0 NormalY=0 NormalZ=1 AngleXU=0 Radius=1.5 StartAngle=4.71239 EndAngle=7.85398
    g15: ArcOfCircle CenterX=-11.49 CenterY=50.5 CenterZ=0 NormalX=0 NormalY=0 NormalZ=1 AngleXU=0 Radius=1.5 StartAngle=4.71239 EndAngle=7.85398
    g16: ArcOfCircle CenterX=-16.28 CenterY=44.75 CenterZ=0 NormalX=0 NormalY=0 NormalZ=1 AngleXU=0 Radius=1.5 StartAngle=4.71239 EndAngle=7.85398
    g17: ArcOfCircle CenterX=-18.2337 CenterY=39 CenterZ=0 NormalX=0 NormalY=0 NormalZ=1 AngleXU=0 Radius=1.5 StartAngle=4.71485 EndAngle=7.85398
    g18: ArcOfCircle CenterX=-16.2837 CenterY=27.25 CenterZ=0 NormalX=0 NormalY=0 NormalZ=1 AngleXU=0 Radius=1.5 StartAngle=4.71485 EndAngle=7.85398
    g19: ArcOfCircle CenterX=-18.2337 CenterY=33 CenterZ=0 NormalX=0 NormalY=0 NormalZ=1 AngleXU=0 Radius=1.5 StartAngle=4.71485 EndAngle=7.85398
    g20: ArcOfCircle CenterX=-11.49 CenterY=21.5 CenterZ=0 NormalX=0 NormalY=0 NormalZ=1 AngleXU=0 Radius=1.5 StartAngle=4.71239 EndAngle=7.85398
    g21: ArcOfCircle CenterX=-1.5 CenterY=4.25 CenterZ=0 NormalX=0 NormalY=0 NormalZ=1 AngleXU=0 Radius=1.5 StartAngle=4.71239 EndAngle=7.85398
    g22: ArcOfCircle CenterX=-1.5 CenterY=10 CenterZ=0 NormalX=0 NormalY=0 NormalZ=1 AngleXU=0 Radius=1.5 StartAngle=4.71239 EndAngle=7.85398
    g23: ArcOfCircle CenterX=-1.5 CenterY=15.75 CenterZ=0 NormalX=0 NormalY=0 NormalZ=1 AngleXU=0 Radius=1.5 StartAngle=4.71239 EndAngle=7.85398
    g24: LineSegment StartX=-49.19 StartY=69.25 StartZ=0 EndX=-1.5 EndY=69.25 EndZ=0
    g25: LineSegment StartX=-49.19 StartY=66.25 StartZ=0 EndX=-1.5 EndY=66.25 EndZ=0
    g26: LineSegment StartX=-49.19 StartY=63.5 StartZ=0 EndX=-1.5 EndY=63.5 EndZ=0
    g27: LineSegment StartX=-49.19 StartY=60.5 StartZ=0 EndX=-1.5 EndY=60.5 EndZ=0
    g28: LineSegment StartX=-49.19 StartY=57.75 StartZ=0 EndX=-1.5 EndY=57.75 EndZ=0
    g29: LineSegment StartX=-49.19 StartY=54.75 StartZ=0 EndX=-1.5 EndY=54.75 EndZ=0
    g30: LineSegment StartX=-49.19 StartY=52 StartZ=0 EndX=-11.49 EndY=52 EndZ=0
    g31: LineSegment StartX=-49.19 StartY=49 StartZ=0 EndX=-11.49 EndY=49 EndZ=0
    g32: LineSegment StartX=-49.19 StartY=46.25 StartZ=0 EndX=-16.28 EndY=46.25 EndZ=0
    g33: LineSegment StartX=-49.19 StartY=43.25 StartZ=0 EndX=-16.28 EndY=43.25 EndZ=0
    g34: LineSegment StartX=-49.19 StartY=40.5 StartZ=0 EndX=-18.2337 EndY=40.5 EndZ=0
    g35: LineSegment StartX=-49.19 StartY=37.5 StartZ=0 EndX=-18.23 EndY=37.5 EndZ=0
    g36: LineSegment StartX=-49.19 StartY=34.5 StartZ=0 EndX=-18.2337 EndY=34.5 EndZ=0
    g37: LineSegment StartX=-49.19 StartY=31.5 StartZ=0 EndX=-18.23 EndY=31.5 EndZ=0
    g38: LineSegment StartX=-49.19 StartY=28.75 StartZ=0 EndX=-16.2837 EndY=28.75 EndZ=0
    g39: LineSegment StartX=-49.19 StartY=25.75 StartZ=0 EndX=-16.28 EndY=25.75 EndZ=0
    g40: LineSegment StartX=-49.19 StartY=23 StartZ=0 EndX=-11.49 EndY=23 EndZ=0
    g41: LineSegment StartX=-49.19 StartY=20 StartZ=0 EndX=-11.49 EndY=20 EndZ=0
    g42: LineSegment StartX=-49.19 StartY=17.25 StartZ=0 EndX=-1.5 EndY=17.25 EndZ=0
    g43: LineSegment StartX=-49.19 StartY=14.25 StartZ=0 EndX=-1.5 EndY=14.25 EndZ=0
    g44: LineSegment StartX=-49.19 StartY=11.5 StartZ=0 EndX=-1.5 EndY=11.5 EndZ=0
    g45: LineSegment StartX=-49.19 StartY=8.5 StartZ=0 EndX=-1.5 EndY=8.5 EndZ=0
    g46: LineSegment StartX=-49.19 StartY=5.75 StartZ=0 EndX=-1.5 EndY=5.75 EndZ=0
    g47: LineSegment StartX=-49.19 StartY=2.75 StartZ=0 EndX=-1.5 EndY=2.75 EndZ=0
  constraints (120):
    c: Vertical(g0)
    c: Distance(g0) = 3
    c: Block(g0)
    c: Vertical(g1)
    c: Distance(g1) = 3
    c: Vertical(g2)
    c: Equal(g0,g2) = 3
    c: Block(g2)
    c: Vertical(g3)
    c: Equal(g1,g3) = 3
    c: Vertical(g4)
    c: Equal(g0,g4) = 3
    c: Block(g4)
    c: Vertical(g5)
    c: Equal(g1,g5) = 3
    c: Vertical(g6)
    c: Equal(g0,g6) = 3
    c: Block(g6)
    c: Vertical(g7)
    c: Equal(g1,g7) = 3
    c: Vertical(g8)
    c: Equal(g0,g8) = 3
    c: Block(g8)
    c: Vertical(g9)
    c: Equal(g1,g9) = 3
    c: Vertical(g10)
    c: Equal(g0,g10) = 3
    c: Block(g10)
    c: Vertical(g11)
    c: Equal(g1,g11) = 3
    c: Block(g12)
    c: Block(g13)
    c: Block(g14)
    c: Block(g15)
    c: Block(g16)
    c: Block(g17)
    c: Block(g18)
    c: Block(g19)
    c: Block(g20)
    c: Block(g21)
    c: Block(g22)
    c: Block(g23)
    c: Block(g11)
    c: Block(g9)
    c: Block(g7)
    c: Block(g5)
    c: Block(g3)
    c: Block(g1)
    c: Coincident(g24,g0)
    c: Coincident(g24,g12)
    c: Horizontal(g24)
    c: Coincident(g25,g0)
    c: Coincident(g25,g12)
    c: Horizontal(g25)
    c: Coincident(g26,g1)
    c: Coincident(g26,g13)
    c: Horizontal(g26)
    c: Coincident(g27,g1)
    c: Coincident(g27,g13)
    c: Horizontal(g27)
    c: Coincident(g28,g2)
    c: Coincident(g28,g14)
    c: Horizontal(g28)
    c: Coincident(g29,g2)
    c: Coincident(g29,g14)
    c: Horizontal(g29)
    c: Coincident(g30,g3)
    c: Coincident(g30,g15)
    c: Horizontal(g30)
    c: Coincident(g31,g3)
    c: Coincident(g31,g15)
    c: Horizontal(g31)
    c: Coincident(g32,g4)
    c: Coincident(g32,g16)
    c: Horizontal(g32)
    c: Coincident(g33,g4)
    c: Coincident(g33,g16)
    c: Horizontal(g33)
    c: Coincident(g34,g5)
    c: Coincident(g34,g17)
    c: Horizontal(g34)
    c: Coincident(g35,g5)
    c: Coincident(g35,g17)
    c: Horizontal(g35)
    c: Coincident(g36,g6)
    c: Coincident(g36,g19)
    c: Horizontal(g36)
    c: Coincident(g37,g6)
    c: Coincident(g37,g19)
    c: Horizontal(g37)
    c: Coincident(g38,g7)
    c: Coincident(g38,g18)
    c: Horizontal(g38)
    c: Coincident(g39,g7)
    c: Coincident(g39,g18)
    c: Horizontal(g39)
    c: Coincident(g40,g8)
    c: Coincident(g40,g20)
    c: Horizontal(g40)
    c: Coincident(g41,g8)
    c: Coincident(g41,g20)
    c: Horizontal(g41)
    c: Coincident(g42,g9)
    c: Coincident(g42,g23)
    c: Horizontal(g42)
    c: Coincident(g43,g9)
    c: Coincident(g43,g23)
    c: Horizontal(g43)
    c: Coincident(g44,g10)
    c: Coincident(g44,g22)
    c: Horizontal(g44)
    c: Coincident(g45,g10)
    c: Coincident(g45,g22)
    c: Horizontal(g45)
    c: Coincident(g46,g11)
    c: Coincident(g46,g21)
    c: Horizontal(g46)
    c: Coincident(g47,g11)
    c: Coincident(g47,g21)
    c: Horizontal(g47)
FEATURE [Sketcher::SketchObject] Sketch031
  FullyConstrained = true
  Placement = pos=(117,19,0) rot=(0.57735,0.57735,0.57735;2.0944rad)
  sketch-geometry (24):
    g0: ArcOfCircle CenterX=-49.19 CenterY=67.75 CenterZ=0 NormalX=0 NormalY=0 NormalZ=1 AngleXU=0 Radius=1.5 StartAngle=1.5708 EndAngle=4.71239
    g1: ArcOfCircle CenterX=-49.19 CenterY=62 CenterZ=0 NormalX=0 NormalY=0 NormalZ=1 AngleXU=0 Radius=1.5 StartAngle=1.5708 EndAngle=4.71239
    g2: ArcOfCircle CenterX=-49.19 CenterY=56.25 CenterZ=0 NormalX=0 NormalY=0 NormalZ=1 AngleXU=0 Radius=1.5 StartAngle=1.5708 EndAngle=4.71239
    g3: ArcOfCircle CenterX=-49.19 CenterY=50.5 CenterZ=0 NormalX=0 NormalY=0 NormalZ=1 AngleXU=0 Radius=1.5 StartAngle=1.5708 EndAngle=4.71239
    g4: ArcOfCircle CenterX=-49.19 CenterY=44.75 CenterZ=0 NormalX=0 NormalY=0 NormalZ=1 AngleXU=0 Radius=1.5 StartAngle=1.5708 EndAngle=4.71239
    g5: ArcOfCircle CenterX=-49.19 CenterY=39 CenterZ=0 NormalX=0 NormalY=0 NormalZ=1 AngleXU=0 Radius=1.5 StartAngle=1.5708 EndAngle=4.71239
    g6: ArcOfCircle CenterX=-49.19 CenterY=33 CenterZ=0 NormalX=0 NormalY=0 NormalZ=1 AngleXU=0 Radius=1.5 StartAngle=1.5708 EndAngle=4.71239
    g7: ArcOfCircle CenterX=-49.19 CenterY=27.25 CenterZ=0 NormalX=0 NormalY=0 NormalZ=1 AngleXU=0 Radius=1.5 StartAngle=1.5708 EndAngle=4.71239
    g8: ArcOfCircle CenterX=-49.19 CenterY=21.5 CenterZ=0 NormalX=0 NormalY=0 NormalZ=1 AngleXU=0 Radius=1.5 StartAngle=1.5708 EndAngle=4.71239
    g9: ArcOfCircle CenterX=-49.19 CenterY=15.75 CenterZ=0 NormalX=0 NormalY=0 NormalZ=1 AngleXU=0 Radius=1.5 StartAngle=1.5708 EndAngle=4.71239
    g10: ArcOfCircle CenterX=-49.19 CenterY=10 CenterZ=0 NormalX=0 NormalY=0 NormalZ=1 AngleXU=0 Radius=1.5 StartAngle=1.5708 EndAngle=4.71239
    g11: ArcOfCircle CenterX=-49.19 CenterY=4.25 CenterZ=0 NormalX=0 NormalY=0 NormalZ=1 AngleXU=0 Radius=1.5 StartAngle=1.5708 EndAngle=4.71239
    g12: LineSegment StartX=-49.19 StartY=69.25 StartZ=0 EndX=-49.19 EndY=66.25 EndZ=0
    g13: LineSegment StartX=-49.19 StartY=63.5 StartZ=0 EndX=-49.19 EndY=60.5 EndZ=0
    g14: LineSegment StartX=-49.19 StartY=57.75 StartZ=0 EndX=-49.19 EndY=54.75 EndZ=0
    g15: LineSegment StartX=-49.19 StartY=52 StartZ=0 EndX=-49.19 EndY=49 EndZ=0
    g16: LineSegment StartX=-49.19 StartY=46.25 StartZ=0 EndX=-49.19 EndY=43.25 EndZ=0
    g17: LineSegment StartX=-49.19 StartY=40.5 StartZ=0 EndX=-49.19 EndY=37.5 EndZ=0
    g18: LineSegment StartX=-49.19 StartY=34.5 StartZ=0 EndX=-49.19 EndY=31.5 EndZ=0
    g19: LineSegment StartX=-49.19 StartY=28.75 StartZ=0 EndX=-49.19 EndY=25.75 EndZ=0
    g20: LineSegment StartX=-49.19 StartY=23 StartZ=0 EndX=-49.19 EndY=20 EndZ=0
    g21: LineSegment StartX=-49.19 StartY=17.25 StartZ=0 EndX=-49.19 EndY=14.25 EndZ=0
    g22: LineSegment StartX=-49.19 StartY=11.5 StartZ=0 EndX=-49.19 EndY=8.5 EndZ=0
    g23: LineSegment StartX=-49.19 StartY=5.75 StartZ=0 EndX=-49.19 EndY=2.75 EndZ=0
  constraints (48):
    c: Block(g0)
    c: Block(g1)
    c: Block(g2)
    c: Block(g3)
    c: Block(g4)
    c: Block(g5)
    c: Block(g6)
    c: Block(g7)
    c: Block(g8)
    c: Block(g9)
    c: Block(g10)
    c: Block(g11)
    c: Coincident(g12,g0)
    c: Coincident(g12,g0)
    c: Vertical(g12)
    c: Vertical(g13)
    c: Coincident(g13,g1)
    c: Vertical(g14)
    c: Coincident(g14,g2)
    c: Vertical(g15)
    c: Coincident(g15,g3)
    c: Vertical(g16)
    c: Coincident(g16,g4)
    c: Vertical(g17)
    c: Coincident(g17,g5)
    c: Vertical(g18)
    c: Coincident(g18,g6)
    c: Vertical(g19)
    c: Coincident(g19,g7)
    c: Vertical(g20)
    c: Coincident(g20,g8)
    c: Vertical(g21)
    c: Coincident(g21,g9)
    c: Vertical(g22)
    c: Coincident(g22,g10)
    c: Vertical(g23)
    c: Coincident(g23,g11)
    c: Block(g23)
    c: Block(g22)
    c: Block(g21)
    c: Block(g20)
    c: Block(g13)
    c: Block(g14)
    c: Block(g15)
    c: Block(g16)
    c: Block(g17)
    c: Block(g18)
    c: Block(g19)
FEATURE [Part::Extrusion] Extrude022
  Base = -> Sketch030
  Dir = (1,-2e-16,2e-16)
  DirMode = 2
  FaceMakerClass = Part::FaceMakerBullseye
  LengthFwd = 19
  LengthRev = 0
  Placement = pos=(-19,0,0) rot=(0,0,1;0rad)
  Solid = true
  Symmetric = false
FEATURE [Part::Fillet] Fillet022
  Base = -> Extrude022
  Edges = 24 edges r=1.49: [Edge6,Edge11,Edge18,Edge23,Edge30,Edge35,Edge42,Edge47,Edge54,Edge59,Edge66,Edge71,Edge78,Edge83,Edge90,Edge95,Edge102,Edge107,Edge114,Edge119,Edge126,Edge131,Edge138,Edge143]
